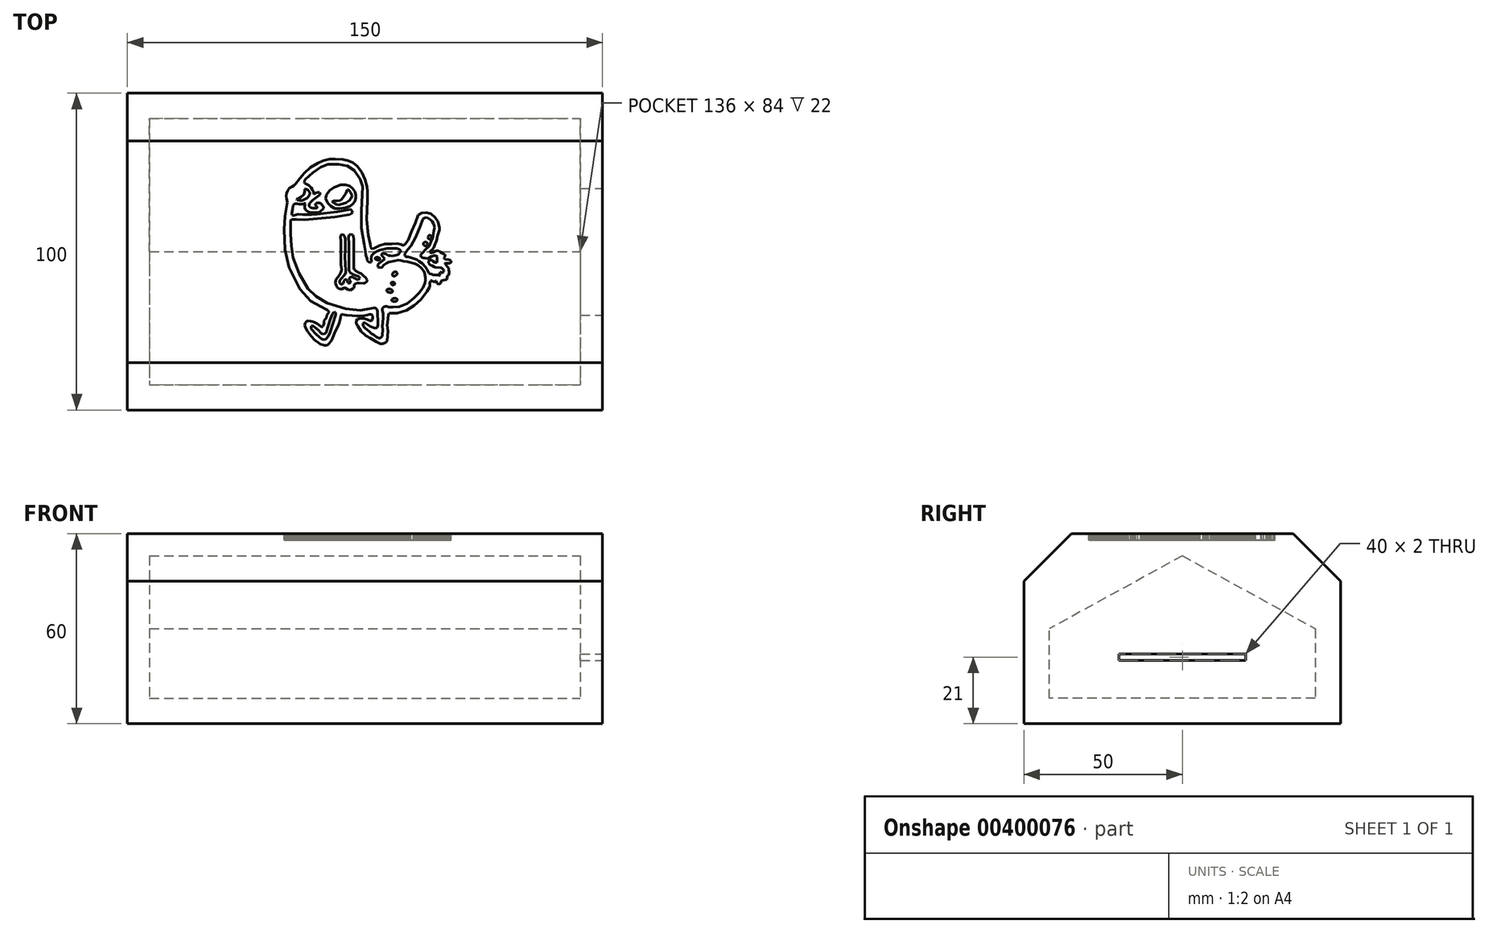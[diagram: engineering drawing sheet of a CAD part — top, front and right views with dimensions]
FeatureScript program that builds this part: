
annotation { "Feature Type Name" : "Feature", "Feature Type Description" : "" }
export const myFeature = defineFeature(function(context is Context, id is Id, definition is map)
    precondition{}
    {
        {
            var Q0;
            Q0=qCreatedBy(makeId("Right.planeOp"),FACE);
            var sketch = newSketch(context, id + "F0", { "sketchPlane" : qUnion([Q0])});
            skLineSegment(sketch, "E0", {"start": v(50, 0) * mm, "end": v(50, -30) * mm});
            skLineSegment(sketch, "E1", {"start": v(50, -30) * mm, "end": v(-50, -30) * mm});
            skLineSegment(sketch, "E2", {"start": v(-50, -30) * mm, "end": v(-50, 30) * mm});
            skLineSegment(sketch, "E3", {"start": v(-50, 30) * mm, "end": v(50, 30) * mm});
            skLineSegment(sketch, "E4", {"start": v(50, 30) * mm, "end": v(50, 0) * mm});
            skLineSegment(sketch, "E5", {"start": v(0, 0) * mm, "end": v(42, 0) * mm});
            skLineSegment(sketch, "E6", {"start": v(42, 0) * mm, "end": v(42, -22) * mm});
            skLineSegment(sketch, "E7", {"start": v(42, -22) * mm, "end": v(-42, -22) * mm});
            skLineSegment(sketch, "E8", {"start": v(-42, -22) * mm, "end": v(-42, 0) * mm});
            skLineSegment(sketch, "E9", {"start": v(0, 30) * mm, "end": v(0, 23) * mm});
            skPoint(sketch, "E9.endSnap0", {"position": v(0, 30) * mm});
            skLineSegment(sketch, "E10", {"start": v(0, 23) * mm, "end": v(-42, 0) * mm});
            skLineSegment(sketch, "E11", {"start": v(0, 23) * mm, "end": v(42, 0) * mm});
            skSolve(sketch);
        }
        {
            var Q0;
            Q0=makeQuery(id+"F0.imprint","IMPRINT",FACE,{"disambiguationData":[TD([[makeQuery(id+"F0.imprint","IMPRINT",EDGE,{"derivedFrom":sQuery(id+"F0.wireOp",EDGE,"E0")}),-1.0]])]});
            extrude(context, id + "F1", {"entities" : qUnion([Q0]), "oppositeDirection" : true, "depth" : 150 * mm});
        }
        {
            var Q0;
            Q0=makeQuery(id+"F1.opExtrude","SWEPT_EDGE",EDGE,{"disambiguationData":[OSD([sQuery(id+"F0.wireOp",EDGE,"E2"),sQuery(id+"F0.wireOp",EDGE,"E3")])]});
            var Q1;
            Q1=makeQuery(id+"F1.opExtrude","SWEPT_EDGE",EDGE,{"disambiguationData":[OSD([sQuery(id+"F0.wireOp",EDGE,"E3"),sQuery(id+"F0.wireOp",EDGE,"E4")])]});
            chamfer(context, id + "F2", {"entities" : qUnion([Q0, Q1]), "width" : 15 * mm, "tangentPropagation" : true});
        }
        {
            var Q0;
            Q0=makeQuery(id+"F1.opExtrude","SWEPT_FACE",FACE,{"disambiguationData":[OSD([sQuery(id+"F0.wireOp",EDGE,"E3")])]});
            var sketch = newSketch(context, id + "F3", { "sketchPlane" : qUnion([Q0])});
            skLineSegment(sketch, "E12", {"start": v(-75, 35) * mm, "end": v(-75, 23.5) * mm});
            skPoint(sketch, "E12.endSnap0", {"position": v(-75, 35) * mm});
            skSolve(sketch);
        }
        {
            var Q0;
            {var subQ0=sQuery(id+"F0.wireOp",EDGE,"E3");var subQ1=makeQuery(id+"F1.opExtrude","CAP_EDGE",EDGE,{"disambiguationData":[OSD([subQ0])],"isStart":true});Q0=makeQuery(id+"F3.imprint","IMPRINT",FACE,{"disambiguationData":[TD([[makeQuery(id+"F3.imprint","IMPRINT",EDGE,{"derivedFrom":subQ1}),1.0]])]});}
            var sketch = newSketch(context, id + "F4", { "sketchPlane" : qUnion([Q0])});
            skLineSegment(sketch, "E13", {"start": v(-75, -30) * mm, "end": v(-105, -30) * mm});
            skLineSegment(sketch, "E14", {"start": v(-105, -30) * mm, "end": v(-105, 30) * mm});
            skLineSegment(sketch, "E15", {"start": v(-105, 30) * mm, "end": v(-45, 30) * mm});
            skLineSegment(sketch, "E16", {"start": v(-71.98, -24.15) * mm, "end": v(-73.3, -23.61) * mm});
            skLineSegment(sketch, "E17", {"start": v(-73.3, -23.61) * mm, "end": v(-74.24, -22.99) * mm});
            skLineSegment(sketch, "E18", {"start": v(-74.24, -22.99) * mm, "end": v(-74.66, -22.67) * mm});
            skLineSegment(sketch, "E19", {"start": v(-74.66, -22.67) * mm, "end": v(-75, -22.48) * mm});
            skLineSegment(sketch, "E20", {"start": v(-75, -22.48) * mm, "end": v(-75.21, -22.4) * mm});
            skLineSegment(sketch, "E21", {"start": v(-75.21, -22.4) * mm, "end": v(-75.4, -22.46) * mm});
            skLineSegment(sketch, "E22", {"start": v(-75.4, -22.46) * mm, "end": v(-75.59, -22.63) * mm});
            skLineSegment(sketch, "E23", {"start": v(-75.59, -22.63) * mm, "end": v(-75.65, -22.8) * mm});
            skLineSegment(sketch, "E24", {"start": v(-75.65, -22.8) * mm, "end": v(-75.62, -23.14) * mm});
            skLineSegment(sketch, "E25", {"start": v(-75.62, -23.14) * mm, "end": v(-75.54, -23.43) * mm});
            skLineSegment(sketch, "E26", {"start": v(-75.54, -23.43) * mm, "end": v(-75.46, -23.63) * mm});
            skLineSegment(sketch, "E27", {"start": v(-75.46, -23.63) * mm, "end": v(-75.27, -23.87) * mm});
            skLineSegment(sketch, "E28", {"start": v(-75.27, -23.87) * mm, "end": v(-74.9, -24.18) * mm});
            skLineSegment(sketch, "E29", {"start": v(-74.9, -24.18) * mm, "end": v(-74.4, -24.63) * mm});
            skLineSegment(sketch, "E30", {"start": v(-74.4, -24.63) * mm, "end": v(-73.63, -25.23) * mm});
            skLineSegment(sketch, "E31", {"start": v(-73.63, -25.23) * mm, "end": v(-73.29, -25.57) * mm});
            skLineSegment(sketch, "E32", {"start": v(-73.29, -25.57) * mm, "end": v(-72.93, -25.92) * mm});
            skLineSegment(sketch, "E33", {"start": v(-72.93, -25.92) * mm, "end": v(-72.2, -26.3) * mm});
            skLineSegment(sketch, "E34", {"start": v(-72.2, -26.3) * mm, "end": v(-71.39, -26.84) * mm});
            skLineSegment(sketch, "E35", {"start": v(-71.39, -26.84) * mm, "end": v(-70.97, -27.16) * mm});
            skLineSegment(sketch, "E36", {"start": v(-70.97, -27.16) * mm, "end": v(-70.75, -27.24) * mm});
            skLineSegment(sketch, "E37", {"start": v(-70.75, -27.24) * mm, "end": v(-70.5, -27.26) * mm});
            skLineSegment(sketch, "E38", {"start": v(-70.5, -27.26) * mm, "end": v(-70.2, -27.24) * mm});
            skLineSegment(sketch, "E39", {"start": v(-70.2, -27.24) * mm, "end": v(-70, -27.13) * mm});
            skLineSegment(sketch, "E40", {"start": v(-70, -27.13) * mm, "end": v(-69.78, -26.94) * mm});
            skLineSegment(sketch, "E41", {"start": v(-69.78, -26.94) * mm, "end": v(-69.61, -26.76) * mm});
            skLineSegment(sketch, "E42", {"start": v(-69.61, -26.76) * mm, "end": v(-69.59, -26.59) * mm});
            skLineSegment(sketch, "E43", {"start": v(-69.59, -26.59) * mm, "end": v(-69.59, -26.2) * mm});
            skLineSegment(sketch, "E44", {"start": v(-69.59, -26.2) * mm, "end": v(-69.38, -24.72) * mm});
            skLineSegment(sketch, "E45", {"start": v(-69.38, -24.72) * mm, "end": v(-69.38, -24.43) * mm});
            skLineSegment(sketch, "E46", {"start": v(-69.38, -24.43) * mm, "end": v(-69.59, -23.58) * mm});
            skLineSegment(sketch, "E47", {"start": v(-69.59, -23.58) * mm, "end": v(-69.59, -23.26) * mm});
            skLineSegment(sketch, "E48", {"start": v(-69.59, -23.26) * mm, "end": v(-69.43, -22.71) * mm});
            skLineSegment(sketch, "E49", {"start": v(-69.43, -22.71) * mm, "end": v(-69.43, -22.14) * mm});
            skLineSegment(sketch, "E50", {"start": v(-69.43, -22.14) * mm, "end": v(-69.32, -21.24) * mm});
            skLineSegment(sketch, "E51", {"start": v(-69.32, -21.24) * mm, "end": v(-69.32, -20.77) * mm});
            skLineSegment(sketch, "E52", {"start": v(-69.32, -20.77) * mm, "end": v(-69.32, -20.27) * mm});
            skLineSegment(sketch, "E53", {"start": v(-69.32, -20.27) * mm, "end": v(-69.32, -19.5) * mm});
            skLineSegment(sketch, "E54", {"start": v(-69.32, -19.5) * mm, "end": v(-69.48, -18.45) * mm});
            skLineSegment(sketch, "E55", {"start": v(-69.48, -18.45) * mm, "end": v(-69.48, -17.95) * mm});
            skLineSegment(sketch, "E56", {"start": v(-69.48, -17.95) * mm, "end": v(-69.36, -17.76) * mm});
            skLineSegment(sketch, "E57", {"start": v(-69.36, -17.76) * mm, "end": v(-69.13, -17.52) * mm});
            skLineSegment(sketch, "E58", {"start": v(-69.13, -17.52) * mm, "end": v(-68.89, -17.36) * mm});
            skLineSegment(sketch, "E59", {"start": v(-68.89, -17.36) * mm, "end": v(-68.51, -17.3) * mm});
            skLineSegment(sketch, "E60", {"start": v(-68.51, -17.3) * mm, "end": v(-68.18, -17.3) * mm});
            skLineSegment(sketch, "E61", {"start": v(-68.18, -17.3) * mm, "end": v(-67.9, -17.38) * mm});
            skLineSegment(sketch, "E62", {"start": v(-67.9, -17.38) * mm, "end": v(-67.48, -17.5) * mm});
            skLineSegment(sketch, "E63", {"start": v(-67.48, -17.5) * mm, "end": v(-66.25, -17.5) * mm});
            skLineSegment(sketch, "E64", {"start": v(-66.25, -17.5) * mm, "end": v(-64.2, -17.36) * mm});
            skLineSegment(sketch, "E65", {"start": v(-64.2, -17.36) * mm, "end": v(-61.7, -16.34) * mm});
            skLineSegment(sketch, "E66", {"start": v(-61.7, -16.34) * mm, "end": v(-59.52, -14.64) * mm});
            skLineSegment(sketch, "E67", {"start": v(-59.52, -14.64) * mm, "end": v(-57.93, -13.11) * mm});
            skLineSegment(sketch, "E68", {"start": v(-57.93, -13.11) * mm, "end": v(-56.69, -11.42) * mm});
            skLineSegment(sketch, "E69", {"start": v(-56.69, -11.42) * mm, "end": v(-56.02, -9.86) * mm});
            skLineSegment(sketch, "E70", {"start": v(-56.02, -9.86) * mm, "end": v(-55.91, -8.97) * mm});
            skLineSegment(sketch, "E71", {"start": v(-55.91, -8.97) * mm, "end": v(-55.91, -8.12) * mm});
            skLineSegment(sketch, "E72", {"start": v(-55.91, -8.12) * mm, "end": v(-56.24, -6.75) * mm});
            skLineSegment(sketch, "E73", {"start": v(-56.24, -6.75) * mm, "end": v(-56.49, -6.12) * mm});
            skLineSegment(sketch, "E74", {"start": v(-56.49, -6.12) * mm, "end": v(-57.35, -5.03) * mm});
            skLineSegment(sketch, "E75", {"start": v(-57.35, -5.03) * mm, "end": v(-58.23, -4.36) * mm});
            skLineSegment(sketch, "E76", {"start": v(-58.23, -4.36) * mm, "end": v(-59.3, -3.85) * mm});
            skLineSegment(sketch, "E77", {"start": v(-59.3, -3.85) * mm, "end": v(-60.49, -3.51) * mm});
            skLineSegment(sketch, "E78", {"start": v(-60.49, -3.51) * mm, "end": v(-61.7, -3.16) * mm});
            skLineSegment(sketch, "E79", {"start": v(-61.7, -3.16) * mm, "end": v(-62.84, -3.03) * mm});
            skLineSegment(sketch, "E80", {"start": v(-62.84, -3.03) * mm, "end": v(-63.68, -2.8) * mm});
            skLineSegment(sketch, "E81", {"start": v(-63.68, -2.8) * mm, "end": v(-64.49, -2.68) * mm});
            skLineSegment(sketch, "E82", {"start": v(-64.49, -2.68) * mm, "end": v(-65.55, -2.88) * mm});
            skLineSegment(sketch, "E83", {"start": v(-65.55, -2.88) * mm, "end": v(-66.86, -3.15) * mm});
            skLineSegment(sketch, "E84", {"start": v(-66.86, -3.15) * mm, "end": v(-67.54, -3.32) * mm});
            skLineSegment(sketch, "E85", {"start": v(-67.54, -3.32) * mm, "end": v(-68.24, -3.7) * mm});
            skLineSegment(sketch, "E86", {"start": v(-68.24, -3.7) * mm, "end": v(-68.99, -4.16) * mm});
            skLineSegment(sketch, "E87", {"start": v(-68.99, -4.16) * mm, "end": v(-69.7, -4.92) * mm});
            skLineSegment(sketch, "E88", {"start": v(-69.7, -4.92) * mm, "end": v(-70.2, -5.03) * mm});
            skLineSegment(sketch, "E89", {"start": v(-70.2, -5.03) * mm, "end": v(-70.78, -4.93) * mm});
            skLineSegment(sketch, "E90", {"start": v(-70.78, -4.93) * mm, "end": v(-70.95, -4.48) * mm});
            skLineSegment(sketch, "E91", {"start": v(-70.95, -4.48) * mm, "end": v(-70.88, -4.03) * mm});
            skLineSegment(sketch, "E92", {"start": v(-70.88, -4.03) * mm, "end": v(-70.5, -3.62) * mm});
            skLineSegment(sketch, "E93", {"start": v(-70.5, -3.62) * mm, "end": v(-69.59, -2.91) * mm});
            skLineSegment(sketch, "E94", {"start": v(-69.59, -2.91) * mm, "end": v(-69.06, -2.52) * mm});
            skLineSegment(sketch, "E95", {"start": v(-69.06, -2.52) * mm, "end": v(-68.87, -2.37) * mm});
            skLineSegment(sketch, "E96", {"start": v(-68.87, -2.37) * mm, "end": v(-68.8, -2.22) * mm});
            skLineSegment(sketch, "E97", {"start": v(-68.8, -2.22) * mm, "end": v(-68.85, -2.09) * mm});
            skLineSegment(sketch, "E98", {"start": v(-68.85, -2.09) * mm, "end": v(-69.21, -1.74) * mm});
            skLineSegment(sketch, "E99", {"start": v(-69.21, -1.74) * mm, "end": v(-69.55, -1.41) * mm});
            skLineSegment(sketch, "E100", {"start": v(-69.55, -1.41) * mm, "end": v(-69.78, -1.12) * mm});
            skLineSegment(sketch, "E101", {"start": v(-69.78, -1.12) * mm, "end": v(-69.78, -0.84) * mm});
            skLineSegment(sketch, "E102", {"start": v(-69.78, -0.84) * mm, "end": v(-69.59, -0.64) * mm});
            skLineSegment(sketch, "E103", {"start": v(-69.59, -0.64) * mm, "end": v(-69.28, -0.53) * mm});
            skLineSegment(sketch, "E104", {"start": v(-69.28, -0.53) * mm, "end": v(-68.85, -0.57) * mm});
            skLineSegment(sketch, "E105", {"start": v(-68.85, -0.57) * mm, "end": v(-68.35, -0.77) * mm});
            skLineSegment(sketch, "E106", {"start": v(-68.35, -0.77) * mm, "end": v(-67.91, -1.05) * mm});
            skLineSegment(sketch, "E107", {"start": v(-67.91, -1.05) * mm, "end": v(-67.66, -1.2) * mm});
            skLineSegment(sketch, "E108", {"start": v(-67.66, -1.2) * mm, "end": v(-67.12, -1.31) * mm});
            skLineSegment(sketch, "E109", {"start": v(-67.12, -1.31) * mm, "end": v(-66.48, -1.36) * mm});
            skLineSegment(sketch, "E110", {"start": v(-66.48, -1.36) * mm, "end": v(-65.85, -1.29) * mm});
            skLineSegment(sketch, "E111", {"start": v(-65.85, -1.29) * mm, "end": v(-65.16, -1.1) * mm});
            skLineSegment(sketch, "E112", {"start": v(-65.16, -1.1) * mm, "end": v(-64.4, -0.83) * mm});
            skLineSegment(sketch, "E113", {"start": v(-64.4, -0.83) * mm, "end": v(-64, -0.41) * mm});
            skLineSegment(sketch, "E114", {"start": v(-64, -0.41) * mm, "end": v(-63.77, -0.05) * mm});
            skLineSegment(sketch, "E115", {"start": v(-63.77, -0.05) * mm, "end": v(-63.67, 0.12) * mm});
            skLineSegment(sketch, "E116", {"start": v(-63.67, 0.12) * mm, "end": v(-63.67, 0.25) * mm});
            skLineSegment(sketch, "E117", {"start": v(-63.67, 0.25) * mm, "end": v(-63.8, 0.42) * mm});
            skLineSegment(sketch, "E118", {"start": v(-63.8, 0.42) * mm, "end": v(-64.05, 0.66) * mm});
            skLineSegment(sketch, "E119", {"start": v(-64.05, 0.66) * mm, "end": v(-64.33, 0.83) * mm});
            skLineSegment(sketch, "E120", {"start": v(-64.33, 0.83) * mm, "end": v(-65, 1.01) * mm});
            skLineSegment(sketch, "E121", {"start": v(-65, 1.01) * mm, "end": v(-67.97, 1.01) * mm});
            skLineSegment(sketch, "E122", {"start": v(-67.97, 1.01) * mm, "end": v(-70.15, 0.5) * mm});
            skLineSegment(sketch, "E123", {"start": v(-70.15, 0.5) * mm, "end": v(-71.15, 0.09) * mm});
            skLineSegment(sketch, "E124", {"start": v(-71.15, 0.09) * mm, "end": v(-72.04, -0.39) * mm});
            skLineSegment(sketch, "E125", {"start": v(-72.04, -0.39) * mm, "end": v(-72.9, -1.27) * mm});
            skLineSegment(sketch, "E126", {"start": v(-72.9, -1.27) * mm, "end": v(-73, -1.55) * mm});
            skLineSegment(sketch, "E127", {"start": v(-73, -1.55) * mm, "end": v(-73.1, -2.31) * mm});
            skLineSegment(sketch, "E128", {"start": v(-73.1, -2.31) * mm, "end": v(-73, -2.78) * mm});
            skLineSegment(sketch, "E129", {"start": v(-73, -2.78) * mm, "end": v(-72.95, -3.06) * mm});
            skLineSegment(sketch, "E130", {"start": v(-72.95, -3.06) * mm, "end": v(-73.07, -3.26) * mm});
            skLineSegment(sketch, "E131", {"start": v(-73.07, -3.26) * mm, "end": v(-73.32, -3.38) * mm});
            skLineSegment(sketch, "E132", {"start": v(-73.32, -3.38) * mm, "end": v(-73.7, -3.3) * mm});
            skLineSegment(sketch, "E133", {"start": v(-73.7, -3.3) * mm, "end": v(-74.07, -3.07) * mm});
            skLineSegment(sketch, "E134", {"start": v(-74.07, -3.07) * mm, "end": v(-74.3, -2.59) * mm});
            skLineSegment(sketch, "E135", {"start": v(-74.3, -2.59) * mm, "end": v(-74.3, -2.1) * mm});
            skLineSegment(sketch, "E136", {"start": v(-74.3, -2.1) * mm, "end": v(-74.7, -1.15) * mm});
            skLineSegment(sketch, "E137", {"start": v(-74.7, -1.15) * mm, "end": v(-74.8, 0) * mm});
            skLineSegment(sketch, "E138", {"start": v(-74.8, 0) * mm, "end": v(-75.18, 2.3) * mm});
            skLineSegment(sketch, "E139", {"start": v(-75.18, 2.3) * mm, "end": v(-76.2, 7.42) * mm});
            skLineSegment(sketch, "E140", {"start": v(-76.2, 7.42) * mm, "end": v(-76.2, 12.88) * mm});
            skLineSegment(sketch, "E141", {"start": v(-76.2, 12.88) * mm, "end": v(-76, 16.85) * mm});
            skLineSegment(sketch, "E142", {"start": v(-76, 16.85) * mm, "end": v(-75.8, 20.59) * mm});
            skLineSegment(sketch, "E143", {"start": v(-75.8, 20.59) * mm, "end": v(-76.53, 22.91) * mm});
            skLineSegment(sketch, "E144", {"start": v(-76.53, 22.91) * mm, "end": v(-78.47, 25.72) * mm});
            skLineSegment(sketch, "E145", {"start": v(-78.47, 25.72) * mm, "end": v(-80.63, 27.07) * mm});
            skLineSegment(sketch, "E146", {"start": v(-80.63, 27.07) * mm, "end": v(-83.35, 27.56) * mm});
            skLineSegment(sketch, "E147", {"start": v(-83.35, 27.56) * mm, "end": v(-86.64, 27.56) * mm});
            skLineSegment(sketch, "E148", {"start": v(-86.64, 27.56) * mm, "end": v(-88.91, 26.63) * mm});
            skLineSegment(sketch, "E149", {"start": v(-88.91, 26.63) * mm, "end": v(-91.46, 24.93) * mm});
            skLineSegment(sketch, "E150", {"start": v(-91.46, 24.93) * mm, "end": v(-93.75, 22.9) * mm});
            skLineSegment(sketch, "E151", {"start": v(-93.75, 22.9) * mm, "end": v(-94.04, 22.5) * mm});
            skLineSegment(sketch, "E152", {"start": v(-94.04, 22.5) * mm, "end": v(-94.19, 22.02) * mm});
            skLineSegment(sketch, "E153", {"start": v(-94.19, 22.02) * mm, "end": v(-94.06, 21.65) * mm});
            skLineSegment(sketch, "E154", {"start": v(-94.06, 21.65) * mm, "end": v(-93.48, 21.4) * mm});
            skLineSegment(sketch, "E155", {"start": v(-93.48, 21.4) * mm, "end": v(-92.7, 20.95) * mm});
            skLineSegment(sketch, "E156", {"start": v(-92.7, 20.95) * mm, "end": v(-92.05, 20.22) * mm});
            skLineSegment(sketch, "E157", {"start": v(-92.05, 20.22) * mm, "end": v(-91.63, 19.6) * mm});
            skLineSegment(sketch, "E158", {"start": v(-91.63, 19.6) * mm, "end": v(-91.26, 18.75) * mm});
            skLineSegment(sketch, "E159", {"start": v(-91.26, 18.75) * mm, "end": v(-91.26, 18.5) * mm});
            skLineSegment(sketch, "E160", {"start": v(-91.26, 18.5) * mm, "end": v(-91.2, 18.3) * mm});
            skLineSegment(sketch, "E161", {"start": v(-91.2, 18.3) * mm, "end": v(-91.07, 18.21) * mm});
            skLineSegment(sketch, "E162", {"start": v(-91.07, 18.21) * mm, "end": v(-90.87, 18.28) * mm});
            skLineSegment(sketch, "E163", {"start": v(-90.87, 18.28) * mm, "end": v(-90.53, 18.5) * mm});
            skLineSegment(sketch, "E164", {"start": v(-90.53, 18.5) * mm, "end": v(-89.92, 18.75) * mm});
            skLineSegment(sketch, "E165", {"start": v(-89.92, 18.75) * mm, "end": v(-89.58, 18.75) * mm});
            skLineSegment(sketch, "E166", {"start": v(-89.58, 18.75) * mm, "end": v(-89.34, 18.63) * mm});
            skLineSegment(sketch, "E167", {"start": v(-89.34, 18.63) * mm, "end": v(-89.23, 18.46) * mm});
            skLineSegment(sketch, "E168", {"start": v(-89.23, 18.46) * mm, "end": v(-89.2, 18.17) * mm});
            skLineSegment(sketch, "E169", {"start": v(-89.2, 18.17) * mm, "end": v(-89.26, 17.96) * mm});
            skLineSegment(sketch, "E170", {"start": v(-89.26, 17.96) * mm, "end": v(-89.44, 17.78) * mm});
            skLineSegment(sketch, "E171", {"start": v(-89.44, 17.78) * mm, "end": v(-90.57, 16.9) * mm});
            skLineSegment(sketch, "E172", {"start": v(-90.57, 16.9) * mm, "end": v(-91.46, 16.22) * mm});
            skLineSegment(sketch, "E173", {"start": v(-91.46, 16.22) * mm, "end": v(-92.4, 15.35) * mm});
            skLineSegment(sketch, "E174", {"start": v(-92.4, 15.35) * mm, "end": v(-92.51, 15.1) * mm});
            skLineSegment(sketch, "E175", {"start": v(-92.51, 15.1) * mm, "end": v(-92.6, 14.76) * mm});
            skLineSegment(sketch, "E176", {"start": v(-92.6, 14.76) * mm, "end": v(-92.6, 14.39) * mm});
            skLineSegment(sketch, "E177", {"start": v(-92.6, 14.39) * mm, "end": v(-92.4, 14.1) * mm});
            skLineSegment(sketch, "E178", {"start": v(-92.4, 14.1) * mm, "end": v(-92.05, 13.83) * mm});
            skLineSegment(sketch, "E179", {"start": v(-92.05, 13.83) * mm, "end": v(-91.56, 13.75) * mm});
            skLineSegment(sketch, "E180", {"start": v(-91.56, 13.75) * mm, "end": v(-90.86, 13.75) * mm});
            skLineSegment(sketch, "E181", {"start": v(-90.86, 13.75) * mm, "end": v(-90.22, 13.75) * mm});
            skLineSegment(sketch, "E182", {"start": v(-90.22, 13.75) * mm, "end": v(-90.12, 13.83) * mm});
            skLineSegment(sketch, "E183", {"start": v(-90.12, 13.83) * mm, "end": v(-90.06, 13.99) * mm});
            skLineSegment(sketch, "E184", {"start": v(-90.06, 13.99) * mm, "end": v(-90.1, 14.08) * mm});
            skLineSegment(sketch, "E185", {"start": v(-90.1, 14.08) * mm, "end": v(-90.36, 14.31) * mm});
            skLineSegment(sketch, "E186", {"start": v(-90.36, 14.31) * mm, "end": v(-90.58, 14.57) * mm});
            skLineSegment(sketch, "E187", {"start": v(-90.58, 14.57) * mm, "end": v(-90.64, 14.84) * mm});
            skLineSegment(sketch, "E188", {"start": v(-90.64, 14.84) * mm, "end": v(-90.6, 15.06) * mm});
            skLineSegment(sketch, "E189", {"start": v(-90.6, 15.06) * mm, "end": v(-90.45, 15.24) * mm});
            skLineSegment(sketch, "E190", {"start": v(-90.45, 15.24) * mm, "end": v(-90.12, 15.37) * mm});
            skLineSegment(sketch, "E191", {"start": v(-90.12, 15.37) * mm, "end": v(-89.72, 15.42) * mm});
            skLineSegment(sketch, "E192", {"start": v(-89.72, 15.42) * mm, "end": v(-89.3, 15.34) * mm});
            skLineSegment(sketch, "E193", {"start": v(-89.3, 15.34) * mm, "end": v(-89.02, 15.25) * mm});
            skLineSegment(sketch, "E194", {"start": v(-89.02, 15.25) * mm, "end": v(-88.87, 15.12) * mm});
            skLineSegment(sketch, "E195", {"start": v(-88.87, 15.12) * mm, "end": v(-88.55, 14.81) * mm});
            skLineSegment(sketch, "E196", {"start": v(-88.55, 14.81) * mm, "end": v(-88.29, 14.45) * mm});
            skLineSegment(sketch, "E197", {"start": v(-88.29, 14.45) * mm, "end": v(-88.13, 13.99) * mm});
            skLineSegment(sketch, "E198", {"start": v(-88.13, 13.99) * mm, "end": v(-88.1, 13.78) * mm});
            skLineSegment(sketch, "E199", {"start": v(-88.1, 13.78) * mm, "end": v(-88.15, 13.62) * mm});
            skLineSegment(sketch, "E200", {"start": v(-88.15, 13.62) * mm, "end": v(-88.36, 13.31) * mm});
            skLineSegment(sketch, "E201", {"start": v(-88.36, 13.31) * mm, "end": v(-88.92, 12.84) * mm});
            skLineSegment(sketch, "E202", {"start": v(-88.92, 12.84) * mm, "end": v(-89.48, 12.46) * mm});
            skLineSegment(sketch, "E203", {"start": v(-89.48, 12.46) * mm, "end": v(-89.66, 12.35) * mm});
            skLineSegment(sketch, "E204", {"start": v(-89.66, 12.35) * mm, "end": v(-90.12, 12.3) * mm});
            skLineSegment(sketch, "E205", {"start": v(-90.12, 12.3) * mm, "end": v(-91.09, 12.3) * mm});
            skLineSegment(sketch, "E206", {"start": v(-91.09, 12.3) * mm, "end": v(-92.27, 12.35) * mm});
            skLineSegment(sketch, "E207", {"start": v(-92.27, 12.35) * mm, "end": v(-93.13, 12.77) * mm});
            skLineSegment(sketch, "E208", {"start": v(-93.13, 12.77) * mm, "end": v(-93.72, 13.25) * mm});
            skLineSegment(sketch, "E209", {"start": v(-93.72, 13.25) * mm, "end": v(-94.02, 13.88) * mm});
            skLineSegment(sketch, "E210", {"start": v(-94.02, 13.88) * mm, "end": v(-94.1, 14.4) * mm});
            skLineSegment(sketch, "E211", {"start": v(-94.1, 14.4) * mm, "end": v(-93.87, 14.95) * mm});
            skLineSegment(sketch, "E212", {"start": v(-93.87, 14.95) * mm, "end": v(-93.82, 15.16) * mm});
            skLineSegment(sketch, "E213", {"start": v(-93.82, 15.16) * mm, "end": v(-93.85, 15.23) * mm});
            skLineSegment(sketch, "E214", {"start": v(-93.85, 15.23) * mm, "end": v(-93.93, 15.25) * mm});
            skLineSegment(sketch, "E215", {"start": v(-93.93, 15.25) * mm, "end": v(-94.06, 15.21) * mm});
            skLineSegment(sketch, "E216", {"start": v(-94.06, 15.21) * mm, "end": v(-94.24, 15.07) * mm});
            skLineSegment(sketch, "E217", {"start": v(-94.24, 15.07) * mm, "end": v(-94.44, 15.03) * mm});
            skLineSegment(sketch, "E218", {"start": v(-94.44, 15.03) * mm, "end": v(-94.87, 15.03) * mm});
            skLineSegment(sketch, "E219", {"start": v(-94.87, 15.03) * mm, "end": v(-95.85, 14.97) * mm});
            skLineSegment(sketch, "E220", {"start": v(-95.85, 14.97) * mm, "end": v(-96.37, 15.09) * mm});
            skLineSegment(sketch, "E221", {"start": v(-96.37, 15.09) * mm, "end": v(-96.9, 15.16) * mm});
            skLineSegment(sketch, "E222", {"start": v(-96.9, 15.16) * mm, "end": v(-97.21, 15.09) * mm});
            skLineSegment(sketch, "E223", {"start": v(-97.21, 15.09) * mm, "end": v(-97.5, 14.88) * mm});
            skLineSegment(sketch, "E224", {"start": v(-97.5, 14.88) * mm, "end": v(-97.77, 14.52) * mm});
            skLineSegment(sketch, "E225", {"start": v(-97.77, 14.52) * mm, "end": v(-97.88, 13.48) * mm});
            skLineSegment(sketch, "E226", {"start": v(-97.88, 13.48) * mm, "end": v(-98.11, 12.04) * mm});
            skLineSegment(sketch, "E227", {"start": v(-98.11, 12.04) * mm, "end": v(-98.07, 11.83) * mm});
            skLineSegment(sketch, "E228", {"start": v(-98.07, 11.83) * mm, "end": v(-97.93, 11.6) * mm});
            skLineSegment(sketch, "E229", {"start": v(-97.93, 11.6) * mm, "end": v(-97.76, 11.48) * mm});
            skLineSegment(sketch, "E230", {"start": v(-97.76, 11.48) * mm, "end": v(-97.47, 11.48) * mm});
            skLineSegment(sketch, "E231", {"start": v(-97.47, 11.48) * mm, "end": v(-96.04, 11.86) * mm});
            skLineSegment(sketch, "E232", {"start": v(-96.04, 11.86) * mm, "end": v(-94.63, 11.75) * mm});
            skLineSegment(sketch, "E233", {"start": v(-94.63, 11.75) * mm, "end": v(-93.17, 11.75) * mm});
            skLineSegment(sketch, "E234", {"start": v(-93.17, 11.75) * mm, "end": v(-91.82, 11.68) * mm});
            skLineSegment(sketch, "E235", {"start": v(-91.82, 11.68) * mm, "end": v(-90.06, 11.8) * mm});
            skLineSegment(sketch, "E236", {"start": v(-90.06, 11.8) * mm, "end": v(-88.1, 12.06) * mm});
            skLineSegment(sketch, "E237", {"start": v(-88.1, 12.06) * mm, "end": v(-83.76, 12.59) * mm});
            skLineSegment(sketch, "E238", {"start": v(-83.76, 12.59) * mm, "end": v(-79.74, 13.3) * mm});
            skLineSegment(sketch, "E239", {"start": v(-79.74, 13.3) * mm, "end": v(-79.4, 13.22) * mm});
            skLineSegment(sketch, "E240", {"start": v(-79.4, 13.22) * mm, "end": v(-79.14, 13) * mm});
            skLineSegment(sketch, "E241", {"start": v(-79.14, 13) * mm, "end": v(-79, 12.69) * mm});
            skLineSegment(sketch, "E242", {"start": v(-79, 12.69) * mm, "end": v(-78.97, 12.38) * mm});
            skLineSegment(sketch, "E243", {"start": v(-78.97, 12.38) * mm, "end": v(-79.09, 12.16) * mm});
            skLineSegment(sketch, "E244", {"start": v(-79.09, 12.16) * mm, "end": v(-79.4, 11.9) * mm});
            skLineSegment(sketch, "E245", {"start": v(-79.4, 11.9) * mm, "end": v(-79.81, 11.7) * mm});
            skLineSegment(sketch, "E246", {"start": v(-79.81, 11.7) * mm, "end": v(-80.64, 11.6) * mm});
            skLineSegment(sketch, "E247", {"start": v(-80.64, 11.6) * mm, "end": v(-84.55, 10.93) * mm});
            skLineSegment(sketch, "E248", {"start": v(-84.55, 10.93) * mm, "end": v(-94.17, 10.06) * mm});
            skLineSegment(sketch, "E249", {"start": v(-94.17, 10.06) * mm, "end": v(-96.58, 10.24) * mm});
            skLineSegment(sketch, "E250", {"start": v(-96.58, 10.24) * mm, "end": v(-98.07, 10.14) * mm});
            skLineSegment(sketch, "E251", {"start": v(-98.07, 10.14) * mm, "end": v(-98.45, 9.9) * mm});
            skLineSegment(sketch, "E252", {"start": v(-98.45, 9.9) * mm, "end": v(-98.52, 9.36) * mm});
            skLineSegment(sketch, "E253", {"start": v(-98.52, 9.36) * mm, "end": v(-98.45, 8.32) * mm});
            skLineSegment(sketch, "E254", {"start": v(-98.45, 8.32) * mm, "end": v(-98.45, 5.66) * mm});
            skLineSegment(sketch, "E255", {"start": v(-98.45, 5.66) * mm, "end": v(-98.2, 1.8) * mm});
            skLineSegment(sketch, "E256", {"start": v(-98.2, 1.8) * mm, "end": v(-97.72, -1.94) * mm});
            skLineSegment(sketch, "E257", {"start": v(-97.72, -1.94) * mm, "end": v(-95.87, -6.83) * mm});
            skLineSegment(sketch, "E258", {"start": v(-95.87, -6.83) * mm, "end": v(-93.01, -11.66) * mm});
            skLineSegment(sketch, "E259", {"start": v(-93.01, -11.66) * mm, "end": v(-90.52, -14.09) * mm});
            skLineSegment(sketch, "E260", {"start": v(-90.52, -14.09) * mm, "end": v(-86.88, -16.22) * mm});
            skLineSegment(sketch, "E261", {"start": v(-86.88, -16.22) * mm, "end": v(-81.1, -17.98) * mm});
            skLineSegment(sketch, "E262", {"start": v(-81.1, -17.98) * mm, "end": v(-76.47, -18.57) * mm});
            skLineSegment(sketch, "E263", {"start": v(-76.47, -18.57) * mm, "end": v(-72.2, -17.82) * mm});
            skLineSegment(sketch, "E264", {"start": v(-72.2, -17.82) * mm, "end": v(-71.83, -17.82) * mm});
            skLineSegment(sketch, "E265", {"start": v(-71.83, -17.82) * mm, "end": v(-71.56, -17.88) * mm});
            skLineSegment(sketch, "E266", {"start": v(-71.56, -17.88) * mm, "end": v(-71.3, -18.12) * mm});
            skLineSegment(sketch, "E267", {"start": v(-71.3, -18.12) * mm, "end": v(-71.14, -18.4) * mm});
            skLineSegment(sketch, "E268", {"start": v(-71.14, -18.4) * mm, "end": v(-71.07, -18.9) * mm});
            skLineSegment(sketch, "E269", {"start": v(-71.07, -18.9) * mm, "end": v(-71.07, -20.2) * mm});
            skLineSegment(sketch, "E270", {"start": v(-71.07, -20.2) * mm, "end": v(-70.98, -21.49) * mm});
            skLineSegment(sketch, "E271", {"start": v(-70.98, -21.49) * mm, "end": v(-70.98, -21.97) * mm});
            skLineSegment(sketch, "E272", {"start": v(-70.98, -21.97) * mm, "end": v(-70.98, -23.26) * mm});
            skLineSegment(sketch, "E273", {"start": v(-70.98, -23.26) * mm, "end": v(-71.03, -23.66) * mm});
            skLineSegment(sketch, "E274", {"start": v(-71.03, -23.66) * mm, "end": v(-71.23, -23.95) * mm});
            skLineSegment(sketch, "E275", {"start": v(-71.23, -23.95) * mm, "end": v(-71.5, -24.12) * mm});
            skLineSegment(sketch, "E276", {"start": v(-71.5, -24.12) * mm, "end": v(-71.72, -24.18) * mm});
            skLineSegment(sketch, "E277", {"start": v(-71.72, -24.18) * mm, "end": v(-71.98, -24.15) * mm});
            skLineSegment(sketch, "E278", {"start": v(-81.15, 4.1) * mm, "end": v(-81.15, 0.56) * mm});
            skLineSegment(sketch, "E279", {"start": v(-81.15, 0.56) * mm, "end": v(-81.32, -1.54) * mm});
            skLineSegment(sketch, "E280", {"start": v(-81.32, -1.54) * mm, "end": v(-81.2, -4.03) * mm});
            skLineSegment(sketch, "E281", {"start": v(-81.2, -4.03) * mm, "end": v(-81.03, -5.77) * mm});
            skLineSegment(sketch, "E282", {"start": v(-81.03, -5.77) * mm, "end": v(-81.03, -6.64) * mm});
            skLineSegment(sketch, "E283", {"start": v(-81.03, -6.64) * mm, "end": v(-81.29, -7.22) * mm});
            skLineSegment(sketch, "E284", {"start": v(-81.29, -7.22) * mm, "end": v(-82.78, -8.8) * mm});
            skLineSegment(sketch, "E285", {"start": v(-82.78, -8.8) * mm, "end": v(-82.98, -9.25) * mm});
            skLineSegment(sketch, "E286", {"start": v(-82.98, -9.25) * mm, "end": v(-83.04, -9.73) * mm});
            skLineSegment(sketch, "E287", {"start": v(-83.04, -9.73) * mm, "end": v(-82.88, -10.05) * mm});
            skLineSegment(sketch, "E288", {"start": v(-82.88, -10.05) * mm, "end": v(-82.6, -10.23) * mm});
            skLineSegment(sketch, "E289", {"start": v(-82.6, -10.23) * mm, "end": v(-82.3, -10.23) * mm});
            skLineSegment(sketch, "E290", {"start": v(-82.3, -10.23) * mm, "end": v(-81.85, -9.97) * mm});
            skLineSegment(sketch, "E291", {"start": v(-81.85, -9.97) * mm, "end": v(-81.74, -9.38) * mm});
            skLineSegment(sketch, "E292", {"start": v(-81.74, -9.38) * mm, "end": v(-81.52, -8.97) * mm});
            skLineSegment(sketch, "E293", {"start": v(-81.52, -8.97) * mm, "end": v(-81.16, -8.75) * mm});
            skLineSegment(sketch, "E294", {"start": v(-81.16, -8.75) * mm, "end": v(-80.91, -8.75) * mm});
            skLineSegment(sketch, "E295", {"start": v(-80.91, -8.75) * mm, "end": v(-80.64, -9.22) * mm});
            skLineSegment(sketch, "E296", {"start": v(-80.64, -9.22) * mm, "end": v(-80.47, -9.65) * mm});
            skLineSegment(sketch, "E297", {"start": v(-80.47, -9.65) * mm, "end": v(-80.29, -9.88) * mm});
            skLineSegment(sketch, "E298", {"start": v(-80.29, -9.88) * mm, "end": v(-80.08, -10) * mm});
            skLineSegment(sketch, "E299", {"start": v(-80.08, -10) * mm, "end": v(-79.76, -9.9) * mm});
            skLineSegment(sketch, "E300", {"start": v(-79.76, -9.9) * mm, "end": v(-79.6, -9.68) * mm});
            skLineSegment(sketch, "E301", {"start": v(-79.6, -9.68) * mm, "end": v(-79.55, -9.36) * mm});
            skLineSegment(sketch, "E302", {"start": v(-79.55, -9.36) * mm, "end": v(-79.77, -8.97) * mm});
            skLineSegment(sketch, "E303", {"start": v(-79.77, -8.97) * mm, "end": v(-79.92, -8.75) * mm});
            skLineSegment(sketch, "E304", {"start": v(-79.92, -8.75) * mm, "end": v(-79.92, -8.39) * mm});
            skLineSegment(sketch, "E305", {"start": v(-79.92, -8.39) * mm, "end": v(-79.7, -8.07) * mm});
            skLineSegment(sketch, "E306", {"start": v(-79.7, -8.07) * mm, "end": v(-79.36, -7.95) * mm});
            skLineSegment(sketch, "E307", {"start": v(-79.36, -7.95) * mm, "end": v(-78.94, -8) * mm});
            skLineSegment(sketch, "E308", {"start": v(-78.94, -8) * mm, "end": v(-78.5, -8.2) * mm});
            skLineSegment(sketch, "E309", {"start": v(-78.5, -8.2) * mm, "end": v(-78.05, -8.51) * mm});
            skLineSegment(sketch, "E310", {"start": v(-78.05, -8.51) * mm, "end": v(-77.55, -8.8) * mm});
            skLineSegment(sketch, "E311", {"start": v(-77.55, -8.8) * mm, "end": v(-77.16, -8.85) * mm});
            skLineSegment(sketch, "E312", {"start": v(-77.16, -8.85) * mm, "end": v(-76.84, -8.67) * mm});
            skLineSegment(sketch, "E313", {"start": v(-76.84, -8.67) * mm, "end": v(-76.65, -8.41) * mm});
            skLineSegment(sketch, "E314", {"start": v(-76.65, -8.41) * mm, "end": v(-76.79, -8.04) * mm});
            skLineSegment(sketch, "E315", {"start": v(-76.79, -8.04) * mm, "end": v(-77.26, -7.7) * mm});
            skLineSegment(sketch, "E316", {"start": v(-77.26, -7.7) * mm, "end": v(-78, -7.52) * mm});
            skLineSegment(sketch, "E317", {"start": v(-78, -7.52) * mm, "end": v(-78.63, -7.23) * mm});
            skLineSegment(sketch, "E318", {"start": v(-78.63, -7.23) * mm, "end": v(-79.5, -6.73) * mm});
            skLineSegment(sketch, "E319", {"start": v(-79.5, -6.73) * mm, "end": v(-79.92, -6.22) * mm});
            skLineSegment(sketch, "E320", {"start": v(-79.92, -6.22) * mm, "end": v(-80.13, -5.77) * mm});
            skLineSegment(sketch, "E321", {"start": v(-80.13, -5.77) * mm, "end": v(-80.13, -3.97) * mm});
            skLineSegment(sketch, "E322", {"start": v(-80.13, -3.97) * mm, "end": v(-80.05, -1.3) * mm});
            skLineSegment(sketch, "E323", {"start": v(-80.05, -1.3) * mm, "end": v(-80.05, 2.5) * mm});
            skLineSegment(sketch, "E324", {"start": v(-80.05, 2.5) * mm, "end": v(-80.26, 4.6) * mm});
            skLineSegment(sketch, "E325", {"start": v(-80.26, 4.6) * mm, "end": v(-79.92, 5.31) * mm});
            skLineSegment(sketch, "E326", {"start": v(-79.92, 5.31) * mm, "end": v(-79.54, 5.47) * mm});
            skLineSegment(sketch, "E327", {"start": v(-79.54, 5.47) * mm, "end": v(-78.97, 5.31) * mm});
            skLineSegment(sketch, "E328", {"start": v(-78.97, 5.31) * mm, "end": v(-78.62, 4.8) * mm});
            skLineSegment(sketch, "E329", {"start": v(-78.62, 4.8) * mm, "end": v(-78.5, 4.02) * mm});
            skLineSegment(sketch, "E330", {"start": v(-78.5, 4.02) * mm, "end": v(-78.5, -3.5) * mm});
            skLineSegment(sketch, "E331", {"start": v(-78.5, -3.5) * mm, "end": v(-78.56, -5.14) * mm});
            skLineSegment(sketch, "E332", {"start": v(-78.56, -5.14) * mm, "end": v(-78.38, -5.63) * mm});
            skLineSegment(sketch, "E333", {"start": v(-78.38, -5.63) * mm, "end": v(-77.94, -6.07) * mm});
            skLineSegment(sketch, "E334", {"start": v(-77.94, -6.07) * mm, "end": v(-77, -6.53) * mm});
            skLineSegment(sketch, "E335", {"start": v(-77, -6.53) * mm, "end": v(-76.13, -6.98) * mm});
            skLineSegment(sketch, "E336", {"start": v(-76.13, -6.98) * mm, "end": v(-75.41, -7.67) * mm});
            skLineSegment(sketch, "E337", {"start": v(-75.41, -7.67) * mm, "end": v(-74.9, -8.13) * mm});
            skLineSegment(sketch, "E338", {"start": v(-74.9, -8.13) * mm, "end": v(-74.36, -8.83) * mm});
            skLineSegment(sketch, "E339", {"start": v(-74.36, -8.83) * mm, "end": v(-74.4, -9.35) * mm});
            skLineSegment(sketch, "E340", {"start": v(-74.4, -9.35) * mm, "end": v(-74.82, -9.75) * mm});
            skLineSegment(sketch, "E341", {"start": v(-74.82, -9.75) * mm, "end": v(-75.41, -9.97) * mm});
            skLineSegment(sketch, "E342", {"start": v(-75.41, -9.97) * mm, "end": v(-76.16, -9.95) * mm});
            skLineSegment(sketch, "E343", {"start": v(-76.16, -9.95) * mm, "end": v(-76.9, -9.92) * mm});
            skLineSegment(sketch, "E344", {"start": v(-76.9, -9.92) * mm, "end": v(-77.4, -9.91) * mm});
            skLineSegment(sketch, "E345", {"start": v(-77.4, -9.91) * mm, "end": v(-78, -10.13) * mm});
            skLineSegment(sketch, "E346", {"start": v(-78, -10.13) * mm, "end": v(-78.37, -10.44) * mm});
            skLineSegment(sketch, "E347", {"start": v(-78.37, -10.44) * mm, "end": v(-78.37, -10.96) * mm});
            skLineSegment(sketch, "E348", {"start": v(-78.37, -10.96) * mm, "end": v(-78.53, -11.52) * mm});
            skLineSegment(sketch, "E349", {"start": v(-78.53, -11.52) * mm, "end": v(-79, -11.85) * mm});
            skLineSegment(sketch, "E350", {"start": v(-79, -11.85) * mm, "end": v(-79.74, -12.13) * mm});
            skLineSegment(sketch, "E351", {"start": v(-79.74, -12.13) * mm, "end": v(-80.48, -11.92) * mm});
            skLineSegment(sketch, "E352", {"start": v(-80.48, -11.92) * mm, "end": v(-81.03, -11.48) * mm});
            skLineSegment(sketch, "E353", {"start": v(-81.03, -11.48) * mm, "end": v(-81.28, -11.35) * mm});
            skLineSegment(sketch, "E354", {"start": v(-81.28, -11.35) * mm, "end": v(-81.62, -11.45) * mm});
            skLineSegment(sketch, "E355", {"start": v(-81.62, -11.45) * mm, "end": v(-82.26, -11.75) * mm});
            skLineSegment(sketch, "E356", {"start": v(-82.26, -11.75) * mm, "end": v(-82.76, -11.83) * mm});
            skLineSegment(sketch, "E357", {"start": v(-82.76, -11.83) * mm, "end": v(-83.27, -11.7) * mm});
            skLineSegment(sketch, "E358", {"start": v(-83.27, -11.7) * mm, "end": v(-83.81, -11.23) * mm});
            skLineSegment(sketch, "E359", {"start": v(-83.81, -11.23) * mm, "end": v(-84.15, -10.55) * mm});
            skLineSegment(sketch, "E360", {"start": v(-84.15, -10.55) * mm, "end": v(-84.4, -9.82) * mm});
            skLineSegment(sketch, "E361", {"start": v(-84.4, -9.82) * mm, "end": v(-84.3, -9.2) * mm});
            skLineSegment(sketch, "E362", {"start": v(-84.3, -9.2) * mm, "end": v(-84.15, -8.79) * mm});
            skLineSegment(sketch, "E363", {"start": v(-84.15, -8.79) * mm, "end": v(-83.16, -7.45) * mm});
            skLineSegment(sketch, "E364", {"start": v(-83.16, -7.45) * mm, "end": v(-82.55, -6.42) * mm});
            skLineSegment(sketch, "E365", {"start": v(-82.55, -6.42) * mm, "end": v(-82.4, -5.67) * mm});
            skLineSegment(sketch, "E366", {"start": v(-82.4, -5.67) * mm, "end": v(-82.64, -4) * mm});
            skLineSegment(sketch, "E367", {"start": v(-82.64, -4) * mm, "end": v(-82.64, -2.1) * mm});
            skLineSegment(sketch, "E368", {"start": v(-82.64, -2.1) * mm, "end": v(-82.64, 0.63) * mm});
            skLineSegment(sketch, "E369", {"start": v(-82.64, 0.63) * mm, "end": v(-82.64, 3.66) * mm});
            skLineSegment(sketch, "E370", {"start": v(-82.64, 3.66) * mm, "end": v(-82.74, 4.26) * mm});
            skLineSegment(sketch, "E371", {"start": v(-82.74, 4.26) * mm, "end": v(-82.77, 4.92) * mm});
            skLineSegment(sketch, "E372", {"start": v(-82.77, 4.92) * mm, "end": v(-82.48, 5.34) * mm});
            skLineSegment(sketch, "E373", {"start": v(-82.48, 5.34) * mm, "end": v(-82.06, 5.4) * mm});
            skLineSegment(sketch, "E374", {"start": v(-82.06, 5.4) * mm, "end": v(-81.7, 5.21) * mm});
            skLineSegment(sketch, "E375", {"start": v(-81.7, 5.21) * mm, "end": v(-81.4, 4.82) * mm});
            skLineSegment(sketch, "E376", {"start": v(-81.4, 4.82) * mm, "end": v(-81.15, 4.1) * mm});
            skLineSegment(sketch, "E377", {"start": v(-87.15, -25.3) * mm, "end": v(-86, -21.52) * mm});
            skLineSegment(sketch, "E378", {"start": v(-86, -21.52) * mm, "end": v(-85.26, -19.64) * mm});
            skLineSegment(sketch, "E379", {"start": v(-85.26, -19.64) * mm, "end": v(-84.99, -19.26) * mm});
            skLineSegment(sketch, "E380", {"start": v(-84.99, -19.26) * mm, "end": v(-84.64, -19.08) * mm});
            skLineSegment(sketch, "E381", {"start": v(-84.64, -19.08) * mm, "end": v(-84.4, -19.16) * mm});
            skLineSegment(sketch, "E382", {"start": v(-84.4, -19.16) * mm, "end": v(-84.24, -19.45) * mm});
            skLineSegment(sketch, "E383", {"start": v(-84.24, -19.45) * mm, "end": v(-84.24, -19.86) * mm});
            skLineSegment(sketch, "E384", {"start": v(-84.24, -19.86) * mm, "end": v(-86.07, -25.52) * mm});
            skLineSegment(sketch, "E385", {"start": v(-86.07, -25.52) * mm, "end": v(-86.56, -26.67) * mm});
            skLineSegment(sketch, "E386", {"start": v(-86.56, -26.67) * mm, "end": v(-87.33, -27.6) * mm});
            skLineSegment(sketch, "E387", {"start": v(-87.33, -27.6) * mm, "end": v(-87.94, -27.8) * mm});
            skLineSegment(sketch, "E388", {"start": v(-87.94, -27.8) * mm, "end": v(-88.75, -27.52) * mm});
            skLineSegment(sketch, "E389", {"start": v(-88.75, -27.52) * mm, "end": v(-90.36, -26.2) * mm});
            skLineSegment(sketch, "E390", {"start": v(-90.36, -26.2) * mm, "end": v(-92.02, -24.4) * mm});
            skLineSegment(sketch, "E391", {"start": v(-92.02, -24.4) * mm, "end": v(-92.02, -23.87) * mm});
            skLineSegment(sketch, "E392", {"start": v(-92.02, -23.87) * mm, "end": v(-91.88, -23.47) * mm});
            skLineSegment(sketch, "E393", {"start": v(-91.88, -23.47) * mm, "end": v(-91.63, -23.34) * mm});
            skLineSegment(sketch, "E394", {"start": v(-91.63, -23.34) * mm, "end": v(-91.33, -23.47) * mm});
            skLineSegment(sketch, "E395", {"start": v(-91.33, -23.47) * mm, "end": v(-90.88, -23.91) * mm});
            skLineSegment(sketch, "E396", {"start": v(-90.88, -23.91) * mm, "end": v(-89.75, -24.8) * mm});
            skLineSegment(sketch, "E397", {"start": v(-89.75, -24.8) * mm, "end": v(-88.83, -25.73) * mm});
            skLineSegment(sketch, "E398", {"start": v(-88.83, -25.73) * mm, "end": v(-88.3, -25.98) * mm});
            skLineSegment(sketch, "E399", {"start": v(-88.3, -25.98) * mm, "end": v(-87.72, -25.87) * mm});
            skLineSegment(sketch, "E400", {"start": v(-87.72, -25.87) * mm, "end": v(-87.36, -25.64) * mm});
            skLineSegment(sketch, "E401", {"start": v(-87.36, -25.64) * mm, "end": v(-87.15, -25.3) * mm});
            skLineSegment(sketch, "E402", {"start": v(-84.84, 20.27) * mm, "end": v(-82.7, 21.08) * mm});
            skLineSegment(sketch, "E403", {"start": v(-82.7, 21.08) * mm, "end": v(-81.14, 21.08) * mm});
            skLineSegment(sketch, "E404", {"start": v(-81.14, 21.08) * mm, "end": v(-79.78, 20.7) * mm});
            skLineSegment(sketch, "E405", {"start": v(-79.78, 20.7) * mm, "end": v(-78.91, 20.01) * mm});
            skLineSegment(sketch, "E406", {"start": v(-78.91, 20.01) * mm, "end": v(-78.2, 19) * mm});
            skLineSegment(sketch, "E407", {"start": v(-78.2, 19) * mm, "end": v(-77.85, 17.86) * mm});
            skLineSegment(sketch, "E408", {"start": v(-77.85, 17.86) * mm, "end": v(-77.85, 16.98) * mm});
            skLineSegment(sketch, "E409", {"start": v(-77.85, 16.98) * mm, "end": v(-78.2, 15.89) * mm});
            skLineSegment(sketch, "E410", {"start": v(-78.2, 15.89) * mm, "end": v(-78.96, 14.97) * mm});
            skLineSegment(sketch, "E411", {"start": v(-78.96, 14.97) * mm, "end": v(-79.75, 14.35) * mm});
            skLineSegment(sketch, "E412", {"start": v(-79.75, 14.35) * mm, "end": v(-81.2, 13.89) * mm});
            skLineSegment(sketch, "E413", {"start": v(-81.2, 13.89) * mm, "end": v(-83.05, 13.6) * mm});
            skLineSegment(sketch, "E414", {"start": v(-83.05, 13.6) * mm, "end": v(-84.5, 13.6) * mm});
            skLineSegment(sketch, "E415", {"start": v(-84.5, 13.6) * mm, "end": v(-85.81, 14.35) * mm});
            skLineSegment(sketch, "E416", {"start": v(-85.81, 14.35) * mm, "end": v(-86.8, 15.44) * mm});
            skLineSegment(sketch, "E417", {"start": v(-86.8, 15.44) * mm, "end": v(-87.4, 16.75) * mm});
            skLineSegment(sketch, "E418", {"start": v(-87.4, 16.75) * mm, "end": v(-87.24, 17.91) * mm});
            skLineSegment(sketch, "E419", {"start": v(-87.24, 17.91) * mm, "end": v(-86.2, 19.32) * mm});
            skLineSegment(sketch, "E420", {"start": v(-86.2, 19.32) * mm, "end": v(-84.84, 20.27) * mm});
            skLineSegment(sketch, "E421", {"start": v(-84.32, 14.97) * mm, "end": v(-83.38, 14.8) * mm});
            skLineSegment(sketch, "E422", {"start": v(-83.38, 14.8) * mm, "end": v(-81.04, 15.41) * mm});
            skLineSegment(sketch, "E423", {"start": v(-81.04, 15.41) * mm, "end": v(-79.9, 16.13) * mm});
            skLineSegment(sketch, "E424", {"start": v(-79.9, 16.13) * mm, "end": v(-79.37, 16.76) * mm});
            skLineSegment(sketch, "E425", {"start": v(-79.37, 16.76) * mm, "end": v(-79.03, 17.73) * mm});
            skLineSegment(sketch, "E426", {"start": v(-79.03, 17.73) * mm, "end": v(-79.57, 18.72) * mm});
            skLineSegment(sketch, "E427", {"start": v(-79.57, 18.72) * mm, "end": v(-80.24, 19.52) * mm});
            skLineSegment(sketch, "E428", {"start": v(-80.24, 19.52) * mm, "end": v(-80.6, 19.52) * mm});
            skLineSegment(sketch, "E429", {"start": v(-80.6, 19.52) * mm, "end": v(-81.04, 18.25) * mm});
            skLineSegment(sketch, "E430", {"start": v(-81.04, 18.25) * mm, "end": v(-82.36, 16.53) * mm});
            skLineSegment(sketch, "E431", {"start": v(-82.36, 16.53) * mm, "end": v(-82.82, 16.1) * mm});
            skLineSegment(sketch, "E432", {"start": v(-82.82, 16.1) * mm, "end": v(-83.86, 15.96) * mm});
            skLineSegment(sketch, "E433", {"start": v(-83.86, 15.96) * mm, "end": v(-84.6, 16.05) * mm});
            skLineSegment(sketch, "E434", {"start": v(-84.6, 16.05) * mm, "end": v(-85.07, 16.05) * mm});
            skLineSegment(sketch, "E435", {"start": v(-85.07, 16.05) * mm, "end": v(-85.35, 15.83) * mm});
            skLineSegment(sketch, "E436", {"start": v(-94.85, 16.1) * mm, "end": v(-93.3, 16.87) * mm});
            skLineSegment(sketch, "E437", {"start": v(-93.3, 16.87) * mm, "end": v(-92.45, 17.77) * mm});
            skLineSegment(sketch, "E438", {"start": v(-92.45, 17.77) * mm, "end": v(-92.36, 18.63) * mm});
            skLineSegment(sketch, "E439", {"start": v(-92.36, 18.63) * mm, "end": v(-93, 19.5) * mm});
            skLineSegment(sketch, "E440", {"start": v(-93, 19.5) * mm, "end": v(-93.81, 19.87) * mm});
            skLineSegment(sketch, "E441", {"start": v(-93.81, 19.87) * mm, "end": v(-93.99, 19.71) * mm});
            skLineSegment(sketch, "E442", {"start": v(-93.99, 19.71) * mm, "end": v(-93.99, 18.9) * mm});
            skLineSegment(sketch, "E443", {"start": v(-93.99, 18.9) * mm, "end": v(-94.28, 18.11) * mm});
            skLineSegment(sketch, "E444", {"start": v(-94.28, 18.11) * mm, "end": v(-95.25, 17.1) * mm});
            skLineSegment(sketch, "E445", {"start": v(-95.25, 17.1) * mm, "end": v(-95.9, 16.76) * mm});
            skLineSegment(sketch, "E446", {"start": v(-95.9, 16.76) * mm, "end": v(-96.5, 16.63) * mm});
            skLineSegment(sketch, "E447", {"start": v(-96.5, 16.63) * mm, "end": v(-96.58, 16.47) * mm});
            skLineSegment(sketch, "E448", {"start": v(-96.58, 16.47) * mm, "end": v(-96.5, 16.3) * mm});
            skLineSegment(sketch, "E449", {"start": v(-96.5, 16.3) * mm, "end": v(-95.71, 16.1) * mm});
            skLineSegment(sketch, "E450", {"start": v(-95.71, 16.1) * mm, "end": v(-94.85, 16.1) * mm});
            skEllipse(sketch, "E451", {"center": v(-71.03, -2.22) * mm, "majorRadius": 0.8 * mm, "minorRadius": 0.43 * mm, "majorAxis": v(0.98, -0.18)});
            skEllipse(sketch, "E452", {"center": v(-65.64, -7.04) * mm, "majorRadius": 0.83 * mm, "minorRadius": 0.6 * mm, "majorAxis": v(-0.84, -0.54)});
            skEllipse(sketch, "E453", {"center": v(-66.18, -10.03) * mm, "majorRadius": 0.6 * mm, "minorRadius": 0.44 * mm, "majorAxis": v(-0.97, 0.26)});
            skEllipse(sketch, "E454", {"center": v(-67.18, -12.36) * mm, "majorRadius": 0.95 * mm, "minorRadius": 0.54 * mm, "majorAxis": v(0.97, -0.24)});
            skEllipse(sketch, "E455", {"center": v(-55.9, 2.44) * mm, "majorRadius": 0.67 * mm, "minorRadius": 0.63 * mm, "majorAxis": v(1, -0.13)});
            skLineSegment(sketch, "E456", {"start": v(-87.18, -18.24) * mm, "end": v(-92.08, -15.61) * mm});
            skLineSegment(sketch, "E457", {"start": v(-92.08, -15.61) * mm, "end": v(-95.59, -11.77) * mm});
            skLineSegment(sketch, "E458", {"start": v(-95.59, -11.77) * mm, "end": v(-98.99, -4.88) * mm});
            skLineSegment(sketch, "E459", {"start": v(-98.99, -4.88) * mm, "end": v(-100.28, 0.67) * mm});
            skLineSegment(sketch, "E460", {"start": v(-100.28, 0.67) * mm, "end": v(-100.54, 6.95) * mm});
            skLineSegment(sketch, "E461", {"start": v(-100.54, 6.95) * mm, "end": v(-100.21, 11.18) * mm});
            skLineSegment(sketch, "E462", {"start": v(-100.21, 11.18) * mm, "end": v(-99.65, 15) * mm});
            skLineSegment(sketch, "E463", {"start": v(-99.65, 15) * mm, "end": v(-99.46, 15.57) * mm});
            skLineSegment(sketch, "E464", {"start": v(-99.46, 15.57) * mm, "end": v(-99.59, 16.14) * mm});
            skLineSegment(sketch, "E465", {"start": v(-99.59, 16.14) * mm, "end": v(-99.81, 16.85) * mm});
            skLineSegment(sketch, "E466", {"start": v(-99.81, 16.85) * mm, "end": v(-99.84, 17.57) * mm});
            skLineSegment(sketch, "E467", {"start": v(-99.84, 17.57) * mm, "end": v(-99.72, 18.38) * mm});
            skLineSegment(sketch, "E468", {"start": v(-99.72, 18.38) * mm, "end": v(-99.35, 19.35) * mm});
            skLineSegment(sketch, "E469", {"start": v(-99.35, 19.35) * mm, "end": v(-98.83, 20.04) * mm});
            skLineSegment(sketch, "E470", {"start": v(-98.83, 20.04) * mm, "end": v(-98.13, 20.5) * mm});
            skLineSegment(sketch, "E471", {"start": v(-98.13, 20.5) * mm, "end": v(-97.5, 20.83) * mm});
            skLineSegment(sketch, "E472", {"start": v(-97.5, 20.83) * mm, "end": v(-96.94, 21.34) * mm});
            skLineSegment(sketch, "E473", {"start": v(-96.94, 21.34) * mm, "end": v(-95.59, 23.19) * mm});
            skLineSegment(sketch, "E474", {"start": v(-95.59, 23.19) * mm, "end": v(-94.17, 24.78) * mm});
            skLineSegment(sketch, "E475", {"start": v(-94.17, 24.78) * mm, "end": v(-92.27, 26.51) * mm});
            skLineSegment(sketch, "E476", {"start": v(-92.27, 26.51) * mm, "end": v(-89.8, 27.96) * mm});
            skLineSegment(sketch, "E477", {"start": v(-89.8, 27.96) * mm, "end": v(-88.14, 28.72) * mm});
            skLineSegment(sketch, "E478", {"start": v(-88.14, 28.72) * mm, "end": v(-86.19, 29.21) * mm});
            skLineSegment(sketch, "E479", {"start": v(-86.19, 29.21) * mm, "end": v(-84.45, 29.28) * mm});
            skLineSegment(sketch, "E480", {"start": v(-84.45, 29.28) * mm, "end": v(-81.96, 29.04) * mm});
            skLineSegment(sketch, "E481", {"start": v(-81.96, 29.04) * mm, "end": v(-80.29, 28.72) * mm});
            skLineSegment(sketch, "E482", {"start": v(-80.29, 28.72) * mm, "end": v(-78.76, 28.1) * mm});
            skLineSegment(sketch, "E483", {"start": v(-78.76, 28.1) * mm, "end": v(-77.4, 26.92) * mm});
            skLineSegment(sketch, "E484", {"start": v(-77.4, 26.92) * mm, "end": v(-76.04, 25.03) * mm});
            skLineSegment(sketch, "E485", {"start": v(-76.04, 25.03) * mm, "end": v(-74.94, 22.78) * mm});
            skLineSegment(sketch, "E486", {"start": v(-74.94, 22.78) * mm, "end": v(-74.32, 20.49) * mm});
            skLineSegment(sketch, "E487", {"start": v(-74.32, 20.49) * mm, "end": v(-74.17, 19.04) * mm});
            skLineSegment(sketch, "E488", {"start": v(-74.17, 19.04) * mm, "end": v(-74.17, 16.2) * mm});
            skLineSegment(sketch, "E489", {"start": v(-74.17, 16.2) * mm, "end": v(-74.43, 10.16) * mm});
            skLineSegment(sketch, "E490", {"start": v(-74.43, 10.16) * mm, "end": v(-74, 5.17) * mm});
            skLineSegment(sketch, "E491", {"start": v(-74, 5.17) * mm, "end": v(-73.4, 2.42) * mm});
            skLineSegment(sketch, "E492", {"start": v(-73.4, 2.42) * mm, "end": v(-73.2, 1.39) * mm});
            skLineSegment(sketch, "E493", {"start": v(-73.2, 1.39) * mm, "end": v(-72.96, 0.98) * mm});
            skLineSegment(sketch, "E494", {"start": v(-72.96, 0.98) * mm, "end": v(-72.62, 0.85) * mm});
            skLineSegment(sketch, "E495", {"start": v(-72.62, 0.85) * mm, "end": v(-71.99, 1.19) * mm});
            skLineSegment(sketch, "E496", {"start": v(-71.99, 1.19) * mm, "end": v(-70.46, 1.96) * mm});
            skLineSegment(sketch, "E497", {"start": v(-70.46, 1.96) * mm, "end": v(-68.7, 2.4) * mm});
            skLineSegment(sketch, "E498", {"start": v(-68.7, 2.4) * mm, "end": v(-66.52, 2.45) * mm});
            skLineSegment(sketch, "E499", {"start": v(-66.52, 2.45) * mm, "end": v(-64.86, 2.57) * mm});
            skLineSegment(sketch, "E500", {"start": v(-64.86, 2.57) * mm, "end": v(-63.7, 2.3) * mm});
            skLineSegment(sketch, "E501", {"start": v(-63.7, 2.3) * mm, "end": v(-63.13, 2.08) * mm});
            skLineSegment(sketch, "E502", {"start": v(-63.13, 2.08) * mm, "end": v(-62.7, 2.08) * mm});
            skLineSegment(sketch, "E503", {"start": v(-62.7, 2.08) * mm, "end": v(-62.27, 2.4) * mm});
            skLineSegment(sketch, "E504", {"start": v(-62.27, 2.4) * mm, "end": v(-61.4, 3.63) * mm});
            skLineSegment(sketch, "E505", {"start": v(-61.4, 3.63) * mm, "end": v(-60.2, 6.55) * mm});
            skLineSegment(sketch, "E506", {"start": v(-60.2, 6.55) * mm, "end": v(-59.14, 9.06) * mm});
            skLineSegment(sketch, "E507", {"start": v(-59.14, 9.06) * mm, "end": v(-58.2, 11.58) * mm});
            skLineSegment(sketch, "E508", {"start": v(-58.2, 11.58) * mm, "end": v(-57.05, 12.15) * mm});
            skLineSegment(sketch, "E509", {"start": v(-57.05, 12.15) * mm, "end": v(-55.72, 12.37) * mm});
            skLineSegment(sketch, "E510", {"start": v(-55.72, 12.37) * mm, "end": v(-54.2, 11.9) * mm});
            skLineSegment(sketch, "E511", {"start": v(-54.2, 11.9) * mm, "end": v(-52.9, 10.83) * mm});
            skLineSegment(sketch, "E512", {"start": v(-52.9, 10.83) * mm, "end": v(-52.04, 9.58) * mm});
            skLineSegment(sketch, "E513", {"start": v(-52.04, 9.58) * mm, "end": v(-51.52, 7.67) * mm});
            skLineSegment(sketch, "E514", {"start": v(-51.52, 7.67) * mm, "end": v(-51.52, 6.82) * mm});
            skLineSegment(sketch, "E515", {"start": v(-51.52, 6.82) * mm, "end": v(-52.07, 4.97) * mm});
            skLineSegment(sketch, "E516", {"start": v(-52.07, 4.97) * mm, "end": v(-52.41, 3.57) * mm});
            skLineSegment(sketch, "E517", {"start": v(-52.41, 3.57) * mm, "end": v(-52.99, 2.07) * mm});
            skLineSegment(sketch, "E518", {"start": v(-52.99, 2.07) * mm, "end": v(-53.27, 1.32) * mm});
            skLineSegment(sketch, "E519", {"start": v(-53.27, 1.32) * mm, "end": v(-53.77, 0.64) * mm});
            skLineSegment(sketch, "E520", {"start": v(-53.77, 0.64) * mm, "end": v(-54.23, 0.22) * mm});
            skLineSegment(sketch, "E521", {"start": v(-54.23, 0.22) * mm, "end": v(-54.42, 0) * mm});
            skLineSegment(sketch, "E522", {"start": v(-54.42, 0) * mm, "end": v(-54.45, -0.21) * mm});
            skLineSegment(sketch, "E523", {"start": v(-54.45, -0.21) * mm, "end": v(-54.35, -0.4) * mm});
            skLineSegment(sketch, "E524", {"start": v(-54.35, -0.4) * mm, "end": v(-54.06, -0.42) * mm});
            skLineSegment(sketch, "E525", {"start": v(-54.06, -0.42) * mm, "end": v(-53.55, -0.21) * mm});
            skLineSegment(sketch, "E526", {"start": v(-53.55, -0.21) * mm, "end": v(-52.84, 0.18) * mm});
            skLineSegment(sketch, "E527", {"start": v(-52.84, 0.18) * mm, "end": v(-52.34, 0.31) * mm});
            skLineSegment(sketch, "E528", {"start": v(-52.34, 0.31) * mm, "end": v(-51.76, 0.24) * mm});
            skLineSegment(sketch, "E529", {"start": v(-51.76, 0.24) * mm, "end": v(-51.2, -0.06) * mm});
            skLineSegment(sketch, "E530", {"start": v(-51.2, -0.06) * mm, "end": v(-50.6, -0.51) * mm});
            skLineSegment(sketch, "E531", {"start": v(-50.6, -0.51) * mm, "end": v(-49.88, -0.85) * mm});
            skLineSegment(sketch, "E532", {"start": v(-49.88, -0.85) * mm, "end": v(-49.67, -1.14) * mm});
            skLineSegment(sketch, "E533", {"start": v(-49.67, -1.14) * mm, "end": v(-49.7, -1.47) * mm});
            skLineSegment(sketch, "E534", {"start": v(-49.7, -1.47) * mm, "end": v(-50.03, -1.93) * mm});
            skLineSegment(sketch, "E535", {"start": v(-50.03, -1.93) * mm, "end": v(-49.98, -2.18) * mm});
            skLineSegment(sketch, "E536", {"start": v(-49.98, -2.18) * mm, "end": v(-49.71, -2.35) * mm});
            skLineSegment(sketch, "E537", {"start": v(-49.71, -2.35) * mm, "end": v(-48.73, -2.48) * mm});
            skLineSegment(sketch, "E538", {"start": v(-48.73, -2.48) * mm, "end": v(-48.2, -2.66) * mm});
            skLineSegment(sketch, "E539", {"start": v(-48.2, -2.66) * mm, "end": v(-47.94, -2.9) * mm});
            skLineSegment(sketch, "E540", {"start": v(-47.94, -2.9) * mm, "end": v(-47.8, -3.22) * mm});
            skLineSegment(sketch, "E541", {"start": v(-47.8, -3.22) * mm, "end": v(-47.87, -3.45) * mm});
            skLineSegment(sketch, "E542", {"start": v(-47.87, -3.45) * mm, "end": v(-48.21, -3.63) * mm});
            skLineSegment(sketch, "E543", {"start": v(-48.21, -3.63) * mm, "end": v(-48.63, -3.7) * mm});
            skLineSegment(sketch, "E544", {"start": v(-48.63, -3.7) * mm, "end": v(-49.21, -3.62) * mm});
            skLineSegment(sketch, "E545", {"start": v(-49.21, -3.62) * mm, "end": v(-49.55, -3.59) * mm});
            skLineSegment(sketch, "E546", {"start": v(-49.55, -3.59) * mm, "end": v(-49.68, -3.63) * mm});
            skLineSegment(sketch, "E547", {"start": v(-49.68, -3.63) * mm, "end": v(-49.71, -3.75) * mm});
            skLineSegment(sketch, "E548", {"start": v(-49.71, -3.75) * mm, "end": v(-49.62, -3.95) * mm});
            skLineSegment(sketch, "E549", {"start": v(-49.62, -3.95) * mm, "end": v(-49.31, -4.33) * mm});
            skLineSegment(sketch, "E550", {"start": v(-49.31, -4.33) * mm, "end": v(-48.95, -4.8) * mm});
            skLineSegment(sketch, "E551", {"start": v(-48.95, -4.8) * mm, "end": v(-48.63, -5.23) * mm});
            skLineSegment(sketch, "E552", {"start": v(-48.63, -5.23) * mm, "end": v(-48.55, -5.68) * mm});
            skLineSegment(sketch, "E553", {"start": v(-48.55, -5.68) * mm, "end": v(-48.47, -6.28) * mm});
            skLineSegment(sketch, "E554", {"start": v(-48.47, -6.28) * mm, "end": v(-48.47, -6.75) * mm});
            skLineSegment(sketch, "E555", {"start": v(-48.47, -6.75) * mm, "end": v(-48.62, -7.34) * mm});
            skLineSegment(sketch, "E556", {"start": v(-48.62, -7.34) * mm, "end": v(-49.02, -7.76) * mm});
            skLineSegment(sketch, "E557", {"start": v(-49.02, -7.76) * mm, "end": v(-49.09, -7.96) * mm});
            skLineSegment(sketch, "E558", {"start": v(-49.09, -7.96) * mm, "end": v(-49.03, -8.16) * mm});
            skLineSegment(sketch, "E559", {"start": v(-49.03, -8.16) * mm, "end": v(-48.96, -8.47) * mm});
            skLineSegment(sketch, "E560", {"start": v(-48.96, -8.47) * mm, "end": v(-49.04, -8.65) * mm});
            skLineSegment(sketch, "E561", {"start": v(-49.04, -8.65) * mm, "end": v(-49.27, -8.83) * mm});
            skLineSegment(sketch, "E562", {"start": v(-49.27, -8.83) * mm, "end": v(-49.62, -8.9) * mm});
            skLineSegment(sketch, "E563", {"start": v(-49.62, -8.9) * mm, "end": v(-50.25, -8.96) * mm});
            skLineSegment(sketch, "E564", {"start": v(-50.25, -8.96) * mm, "end": v(-50.74, -9.07) * mm});
            skLineSegment(sketch, "E565", {"start": v(-50.74, -9.07) * mm, "end": v(-50.9, -9.14) * mm});
            skLineSegment(sketch, "E566", {"start": v(-50.9, -9.14) * mm, "end": v(-51.01, -9.3) * mm});
            skLineSegment(sketch, "E567", {"start": v(-51.01, -9.3) * mm, "end": v(-51.01, -9.54) * mm});
            skLineSegment(sketch, "E568", {"start": v(-51.01, -9.54) * mm, "end": v(-51.12, -9.83) * mm});
            skLineSegment(sketch, "E569", {"start": v(-51.12, -9.83) * mm, "end": v(-51.24, -9.99) * mm});
            skLineSegment(sketch, "E570", {"start": v(-51.24, -9.99) * mm, "end": v(-51.52, -10.16) * mm});
            skLineSegment(sketch, "E571", {"start": v(-51.52, -10.16) * mm, "end": v(-51.8, -10.24) * mm});
            skLineSegment(sketch, "E572", {"start": v(-51.8, -10.24) * mm, "end": v(-52.02, -10.2) * mm});
            skLineSegment(sketch, "E573", {"start": v(-52.02, -10.2) * mm, "end": v(-52.23, -10.03) * mm});
            skLineSegment(sketch, "E574", {"start": v(-52.23, -10.03) * mm, "end": v(-52.36, -9.73) * mm});
            skLineSegment(sketch, "E575", {"start": v(-52.36, -9.73) * mm, "end": v(-52.41, -9.48) * mm});
            skLineSegment(sketch, "E576", {"start": v(-52.41, -9.48) * mm, "end": v(-52.5, -9.3) * mm});
            skLineSegment(sketch, "E577", {"start": v(-52.5, -9.3) * mm, "end": v(-52.66, -9.3) * mm});
            skLineSegment(sketch, "E578", {"start": v(-52.66, -9.3) * mm, "end": v(-52.91, -9.36) * mm});
            skLineSegment(sketch, "E579", {"start": v(-52.91, -9.36) * mm, "end": v(-53.16, -9.44) * mm});
            skLineSegment(sketch, "E580", {"start": v(-53.16, -9.44) * mm, "end": v(-53.34, -9.45) * mm});
            skLineSegment(sketch, "E581", {"start": v(-53.34, -9.45) * mm, "end": v(-53.53, -9.35) * mm});
            skLineSegment(sketch, "E582", {"start": v(-53.53, -9.35) * mm, "end": v(-53.73, -9.2) * mm});
            skLineSegment(sketch, "E583", {"start": v(-53.73, -9.2) * mm, "end": v(-53.91, -9.16) * mm});
            skLineSegment(sketch, "E584", {"start": v(-53.91, -9.16) * mm, "end": v(-54.07, -9.17) * mm});
            skLineSegment(sketch, "E585", {"start": v(-54.07, -9.17) * mm, "end": v(-54.23, -9.3) * mm});
            skLineSegment(sketch, "E586", {"start": v(-54.23, -9.3) * mm, "end": v(-54.45, -9.52) * mm});
            skLineSegment(sketch, "E587", {"start": v(-54.45, -9.52) * mm, "end": v(-54.52, -9.91) * mm});
            skLineSegment(sketch, "E588", {"start": v(-54.52, -9.91) * mm, "end": v(-54.52, -10.51) * mm});
            skLineSegment(sketch, "E589", {"start": v(-54.52, -10.51) * mm, "end": v(-54.52, -10.9) * mm});
            skLineSegment(sketch, "E590", {"start": v(-54.52, -10.9) * mm, "end": v(-54.65, -11.3) * mm});
            skLineSegment(sketch, "E591", {"start": v(-54.65, -11.3) * mm, "end": v(-55.46, -12.6) * mm});
            skLineSegment(sketch, "E592", {"start": v(-55.46, -12.6) * mm, "end": v(-57.3, -15.04) * mm});
            skLineSegment(sketch, "E593", {"start": v(-57.3, -15.04) * mm, "end": v(-59.48, -16.94) * mm});
            skLineSegment(sketch, "E594", {"start": v(-59.48, -16.94) * mm, "end": v(-61.95, -18.5) * mm});
            skLineSegment(sketch, "E595", {"start": v(-61.95, -18.5) * mm, "end": v(-64.87, -19.36) * mm});
            skLineSegment(sketch, "E596", {"start": v(-64.87, -19.36) * mm, "end": v(-66.8, -19.36) * mm});
            skLineSegment(sketch, "E597", {"start": v(-66.8, -19.36) * mm, "end": v(-67.31, -19.45) * mm});
            skLineSegment(sketch, "E598", {"start": v(-67.31, -19.45) * mm, "end": v(-67.5, -19.6) * mm});
            skLineSegment(sketch, "E599", {"start": v(-67.5, -19.6) * mm, "end": v(-67.57, -19.89) * mm});
            skLineSegment(sketch, "E600", {"start": v(-67.57, -19.89) * mm, "end": v(-67.88, -22.38) * mm});
            skLineSegment(sketch, "E601", {"start": v(-67.88, -22.38) * mm, "end": v(-68.02, -23.2) * mm});
            skLineSegment(sketch, "E602", {"start": v(-68.02, -23.2) * mm, "end": v(-67.75, -25.09) * mm});
            skLineSegment(sketch, "E603", {"start": v(-67.75, -25.09) * mm, "end": v(-67.93, -26.5) * mm});
            skLineSegment(sketch, "E604", {"start": v(-67.93, -26.5) * mm, "end": v(-68.06, -28.17) * mm});
            skLineSegment(sketch, "E605", {"start": v(-68.06, -28.17) * mm, "end": v(-68.54, -28.72) * mm});
            skLineSegment(sketch, "E606", {"start": v(-68.54, -28.72) * mm, "end": v(-69.36, -29.07) * mm});
            skLineSegment(sketch, "E607", {"start": v(-69.36, -29.07) * mm, "end": v(-70.14, -29.05) * mm});
            skLineSegment(sketch, "E608", {"start": v(-70.14, -29.05) * mm, "end": v(-71.47, -28.48) * mm});
            skLineSegment(sketch, "E609", {"start": v(-71.47, -28.48) * mm, "end": v(-73.37, -27.35) * mm});
            skLineSegment(sketch, "E610", {"start": v(-73.37, -27.35) * mm, "end": v(-74.74, -26.57) * mm});
            skLineSegment(sketch, "E611", {"start": v(-74.74, -26.57) * mm, "end": v(-76.24, -25.09) * mm});
            skLineSegment(sketch, "E612", {"start": v(-76.24, -25.09) * mm, "end": v(-77.3, -23.53) * mm});
            skLineSegment(sketch, "E613", {"start": v(-77.3, -23.53) * mm, "end": v(-77.8, -22.58) * mm});
            skLineSegment(sketch, "E614", {"start": v(-77.8, -22.58) * mm, "end": v(-77.76, -21.9) * mm});
            skLineSegment(sketch, "E615", {"start": v(-77.76, -21.9) * mm, "end": v(-77.34, -21.38) * mm});
            skLineSegment(sketch, "E616", {"start": v(-77.34, -21.38) * mm, "end": v(-76.86, -21.14) * mm});
            skLineSegment(sketch, "E617", {"start": v(-76.86, -21.14) * mm, "end": v(-76.4, -21) * mm});
            skLineSegment(sketch, "E618", {"start": v(-76.4, -21) * mm, "end": v(-75.39, -21.08) * mm});
            skLineSegment(sketch, "E619", {"start": v(-75.39, -21.08) * mm, "end": v(-74.54, -21.26) * mm});
            skLineSegment(sketch, "E620", {"start": v(-74.54, -21.26) * mm, "end": v(-73.65, -21.73) * mm});
            skLineSegment(sketch, "E621", {"start": v(-73.65, -21.73) * mm, "end": v(-73.36, -21.87) * mm});
            skLineSegment(sketch, "E622", {"start": v(-73.36, -21.87) * mm, "end": v(-73, -21.83) * mm});
            skLineSegment(sketch, "E623", {"start": v(-73, -21.83) * mm, "end": v(-72.78, -21.65) * mm});
            skLineSegment(sketch, "E624", {"start": v(-72.78, -21.65) * mm, "end": v(-72.67, -21.48) * mm});
            skLineSegment(sketch, "E625", {"start": v(-72.67, -21.48) * mm, "end": v(-72.6, -20.78) * mm});
            skLineSegment(sketch, "E626", {"start": v(-72.6, -20.78) * mm, "end": v(-72.6, -20.3) * mm});
            skLineSegment(sketch, "E627", {"start": v(-72.6, -20.3) * mm, "end": v(-72.84, -19.96) * mm});
            skLineSegment(sketch, "E628", {"start": v(-72.84, -19.96) * mm, "end": v(-73.16, -19.75) * mm});
            skLineSegment(sketch, "E629", {"start": v(-73.16, -19.75) * mm, "end": v(-73.63, -19.8) * mm});
            skLineSegment(sketch, "E630", {"start": v(-73.63, -19.8) * mm, "end": v(-74.44, -20) * mm});
            skLineSegment(sketch, "E631", {"start": v(-74.44, -20) * mm, "end": v(-75.74, -20.25) * mm});
            skLineSegment(sketch, "E632", {"start": v(-75.74, -20.25) * mm, "end": v(-77.5, -20.28) * mm});
            skLineSegment(sketch, "E633", {"start": v(-77.5, -20.28) * mm, "end": v(-79.06, -20.19) * mm});
            skLineSegment(sketch, "E634", {"start": v(-79.06, -20.19) * mm, "end": v(-80.89, -20.03) * mm});
            skLineSegment(sketch, "E635", {"start": v(-80.89, -20.03) * mm, "end": v(-82.17, -19.77) * mm});
            skLineSegment(sketch, "E636", {"start": v(-82.17, -19.77) * mm, "end": v(-82.4, -19.85) * mm});
            skLineSegment(sketch, "E637", {"start": v(-82.4, -19.85) * mm, "end": v(-82.59, -20.1) * mm});
            skLineSegment(sketch, "E638", {"start": v(-82.59, -20.1) * mm, "end": v(-82.77, -20.93) * mm});
            skLineSegment(sketch, "E639", {"start": v(-82.77, -20.93) * mm, "end": v(-83.16, -22.4) * mm});
            skLineSegment(sketch, "E640", {"start": v(-83.16, -22.4) * mm, "end": v(-83.65, -23.75) * mm});
            skLineSegment(sketch, "E641", {"start": v(-83.65, -23.75) * mm, "end": v(-84.37, -25.08) * mm});
            skLineSegment(sketch, "E642", {"start": v(-84.37, -25.08) * mm, "end": v(-85.4, -27.63) * mm});
            skLineSegment(sketch, "E643", {"start": v(-85.4, -27.63) * mm, "end": v(-85.7, -28.23) * mm});
            skLineSegment(sketch, "E644", {"start": v(-85.7, -28.23) * mm, "end": v(-86.57, -29.25) * mm});
            skLineSegment(sketch, "E645", {"start": v(-86.57, -29.25) * mm, "end": v(-86.84, -29.42) * mm});
            skLineSegment(sketch, "E646", {"start": v(-86.84, -29.42) * mm, "end": v(-87.27, -29.58) * mm});
            skLineSegment(sketch, "E647", {"start": v(-87.27, -29.58) * mm, "end": v(-87.82, -29.57) * mm});
            skLineSegment(sketch, "E648", {"start": v(-87.82, -29.57) * mm, "end": v(-88.24, -29.49) * mm});
            skLineSegment(sketch, "E649", {"start": v(-88.24, -29.49) * mm, "end": v(-89.02, -29.14) * mm});
            skLineSegment(sketch, "E650", {"start": v(-89.02, -29.14) * mm, "end": v(-89.55, -28.84) * mm});
            skLineSegment(sketch, "E651", {"start": v(-89.55, -28.84) * mm, "end": v(-90.81, -27.86) * mm});
            skLineSegment(sketch, "E652", {"start": v(-90.81, -27.86) * mm, "end": v(-92.05, -26.69) * mm});
            skLineSegment(sketch, "E653", {"start": v(-92.05, -26.69) * mm, "end": v(-93.19, -25.17) * mm});
            skLineSegment(sketch, "E654", {"start": v(-93.19, -25.17) * mm, "end": v(-93.8, -24) * mm});
            skLineSegment(sketch, "E655", {"start": v(-93.8, -24) * mm, "end": v(-94.03, -23.23) * mm});
            skLineSegment(sketch, "E656", {"start": v(-94.03, -23.23) * mm, "end": v(-93.96, -22.6) * mm});
            skLineSegment(sketch, "E657", {"start": v(-93.96, -22.6) * mm, "end": v(-93.55, -22.1) * mm});
            skLineSegment(sketch, "E658", {"start": v(-93.55, -22.1) * mm, "end": v(-92.97, -21.88) * mm});
            skLineSegment(sketch, "E659", {"start": v(-92.97, -21.88) * mm, "end": v(-92.14, -21.94) * mm});
            skLineSegment(sketch, "E660", {"start": v(-92.14, -21.94) * mm, "end": v(-91.5, -22.06) * mm});
            skLineSegment(sketch, "E661", {"start": v(-91.5, -22.06) * mm, "end": v(-90.8, -22.34) * mm});
            skLineSegment(sketch, "E662", {"start": v(-90.8, -22.34) * mm, "end": v(-90.12, -22.7) * mm});
            skLineSegment(sketch, "E663", {"start": v(-90.12, -22.7) * mm, "end": v(-89.6, -23.09) * mm});
            skLineSegment(sketch, "E664", {"start": v(-89.6, -23.09) * mm, "end": v(-89.12, -23.52) * mm});
            skLineSegment(sketch, "E665", {"start": v(-89.12, -23.52) * mm, "end": v(-88.78, -23.77) * mm});
            skLineSegment(sketch, "E666", {"start": v(-88.78, -23.77) * mm, "end": v(-88.52, -23.77) * mm});
            skLineSegment(sketch, "E667", {"start": v(-88.52, -23.77) * mm, "end": v(-88.3, -23.61) * mm});
            skLineSegment(sketch, "E668", {"start": v(-88.3, -23.61) * mm, "end": v(-88.14, -23.4) * mm});
            skLineSegment(sketch, "E669", {"start": v(-88.14, -23.4) * mm, "end": v(-88.07, -23.22) * mm});
            skLineSegment(sketch, "E670", {"start": v(-88.07, -23.22) * mm, "end": v(-87.98, -22.63) * mm});
            skLineSegment(sketch, "E671", {"start": v(-87.98, -22.63) * mm, "end": v(-87.9, -21.88) * mm});
            skLineSegment(sketch, "E672", {"start": v(-87.9, -21.88) * mm, "end": v(-87.56, -21.3) * mm});
            skLineSegment(sketch, "E673", {"start": v(-87.56, -21.3) * mm, "end": v(-87.2, -20.9) * mm});
            skLineSegment(sketch, "E674", {"start": v(-87.2, -20.9) * mm, "end": v(-87.11, -20.1) * mm});
            skLineSegment(sketch, "E675", {"start": v(-87.11, -20.1) * mm, "end": v(-86.47, -19.13) * mm});
            skLineSegment(sketch, "E676", {"start": v(-86.47, -19.13) * mm, "end": v(-86.47, -18.94) * mm});
            skLineSegment(sketch, "E677", {"start": v(-86.47, -18.94) * mm, "end": v(-86.61, -18.7) * mm});
            skLineSegment(sketch, "E678", {"start": v(-86.61, -18.7) * mm, "end": v(-86.84, -18.43) * mm});
            skLineSegment(sketch, "E679", {"start": v(-86.84, -18.43) * mm, "end": v(-87.18, -18.24) * mm});
            skLineSegment(sketch, "E680", {"start": v(-61.56, 0.61) * mm, "end": v(-60.45, 1.82) * mm});
            skLineSegment(sketch, "E681", {"start": v(-60.45, 1.82) * mm, "end": v(-58.92, 4.54) * mm});
            skLineSegment(sketch, "E682", {"start": v(-58.92, 4.54) * mm, "end": v(-57.48, 8.28) * mm});
            skLineSegment(sketch, "E683", {"start": v(-57.48, 8.28) * mm, "end": v(-56.86, 10.06) * mm});
            skLineSegment(sketch, "E684", {"start": v(-56.86, 10.06) * mm, "end": v(-56.6, 10.4) * mm});
            skLineSegment(sketch, "E685", {"start": v(-56.6, 10.4) * mm, "end": v(-56.12, 10.66) * mm});
            skLineSegment(sketch, "E686", {"start": v(-56.12, 10.66) * mm, "end": v(-55.48, 10.76) * mm});
            skLineSegment(sketch, "E687", {"start": v(-55.48, 10.76) * mm, "end": v(-55.01, 10.55) * mm});
            skLineSegment(sketch, "E688", {"start": v(-55.01, 10.55) * mm, "end": v(-54.27, 10.05) * mm});
            skLineSegment(sketch, "E689", {"start": v(-54.27, 10.05) * mm, "end": v(-53.75, 9.58) * mm});
            skLineSegment(sketch, "E690", {"start": v(-53.75, 9.58) * mm, "end": v(-53.38, 8.92) * mm});
            skLineSegment(sketch, "E691", {"start": v(-53.38, 8.92) * mm, "end": v(-53.13, 8.1) * mm});
            skLineSegment(sketch, "E692", {"start": v(-53.13, 8.1) * mm, "end": v(-53.05, 7.63) * mm});
            skLineSegment(sketch, "E693", {"start": v(-53.05, 7.63) * mm, "end": v(-53.12, 7.1) * mm});
            skLineSegment(sketch, "E694", {"start": v(-53.12, 7.1) * mm, "end": v(-53.27, 6.58) * mm});
            skLineSegment(sketch, "E695", {"start": v(-53.27, 6.58) * mm, "end": v(-53.5, 4.99) * mm});
            skLineSegment(sketch, "E696", {"start": v(-53.5, 4.99) * mm, "end": v(-53.6, 4.36) * mm});
            skLineSegment(sketch, "E697", {"start": v(-53.6, 4.36) * mm, "end": v(-54.16, 3.16) * mm});
            skLineSegment(sketch, "E698", {"start": v(-54.16, 3.16) * mm, "end": v(-54.5, 2.2) * mm});
            skLineSegment(sketch, "E699", {"start": v(-54.5, 2.2) * mm, "end": v(-54.83, 1.64) * mm});
            skLineSegment(sketch, "E700", {"start": v(-54.83, 1.64) * mm, "end": v(-55.94, 0.6) * mm});
            skLineSegment(sketch, "E701", {"start": v(-55.94, 0.6) * mm, "end": v(-56.64, -0.18) * mm});
            skLineSegment(sketch, "E702", {"start": v(-56.64, -0.18) * mm, "end": v(-57.26, -0.72) * mm});
            skLineSegment(sketch, "E703", {"start": v(-57.26, -0.72) * mm, "end": v(-57.38, -0.93) * mm});
            skLineSegment(sketch, "E704", {"start": v(-57.38, -0.93) * mm, "end": v(-57.4, -1.12) * mm});
            skLineSegment(sketch, "E705", {"start": v(-57.4, -1.12) * mm, "end": v(-57.28, -1.44) * mm});
            skLineSegment(sketch, "E706", {"start": v(-57.28, -1.44) * mm, "end": v(-57.01, -1.75) * mm});
            skLineSegment(sketch, "E707", {"start": v(-57.01, -1.75) * mm, "end": v(-56.8, -1.89) * mm});
            skLineSegment(sketch, "E708", {"start": v(-56.8, -1.89) * mm, "end": v(-56.46, -1.97) * mm});
            skLineSegment(sketch, "E709", {"start": v(-56.46, -1.97) * mm, "end": v(-56.08, -2.04) * mm});
            skLineSegment(sketch, "E710", {"start": v(-56.08, -2.04) * mm, "end": v(-55.6, -2.16) * mm});
            skLineSegment(sketch, "E711", {"start": v(-55.6, -2.16) * mm, "end": v(-55.44, -2.21) * mm});
            skLineSegment(sketch, "E712", {"start": v(-55.44, -2.21) * mm, "end": v(-55.2, -2.12) * mm});
            skLineSegment(sketch, "E713", {"start": v(-55.2, -2.12) * mm, "end": v(-54.64, -1.89) * mm});
            skLineSegment(sketch, "E714", {"start": v(-54.64, -1.89) * mm, "end": v(-54.05, -1.54) * mm});
            skLineSegment(sketch, "E715", {"start": v(-54.05, -1.54) * mm, "end": v(-53.31, -1.29) * mm});
            skLineSegment(sketch, "E716", {"start": v(-53.31, -1.29) * mm, "end": v(-52.88, -1.23) * mm});
            skLineSegment(sketch, "E717", {"start": v(-52.88, -1.23) * mm, "end": v(-52.45, -1.38) * mm});
            skLineSegment(sketch, "E718", {"start": v(-52.45, -1.38) * mm, "end": v(-52.23, -1.47) * mm});
            skLineSegment(sketch, "E719", {"start": v(-52.23, -1.47) * mm, "end": v(-52.14, -1.57) * mm});
            skLineSegment(sketch, "E720", {"start": v(-52.14, -1.57) * mm, "end": v(-52.14, -1.68) * mm});
            skLineSegment(sketch, "E721", {"start": v(-52.14, -1.68) * mm, "end": v(-52.26, -1.82) * mm});
            skLineSegment(sketch, "E722", {"start": v(-52.26, -1.82) * mm, "end": v(-52.22, -2.29) * mm});
            skLineSegment(sketch, "E723", {"start": v(-52.22, -2.29) * mm, "end": v(-52.3, -2.85) * mm});
            skLineSegment(sketch, "E724", {"start": v(-52.3, -2.85) * mm, "end": v(-52.27, -3.28) * mm});
            skLineSegment(sketch, "E725", {"start": v(-52.27, -3.28) * mm, "end": v(-52.29, -3.42) * mm});
            skLineSegment(sketch, "E726", {"start": v(-52.29, -3.42) * mm, "end": v(-52.4, -3.45) * mm});
            skLineSegment(sketch, "E727", {"start": v(-52.4, -3.45) * mm, "end": v(-52.87, -3.38) * mm});
            skLineSegment(sketch, "E728", {"start": v(-52.87, -3.38) * mm, "end": v(-53.55, -2.99) * mm});
            skLineSegment(sketch, "E729", {"start": v(-53.55, -2.99) * mm, "end": v(-53.78, -2.75) * mm});
            skLineSegment(sketch, "E730", {"start": v(-53.78, -2.75) * mm, "end": v(-53.97, -2.63) * mm});
            skLineSegment(sketch, "E731", {"start": v(-53.97, -2.63) * mm, "end": v(-54.15, -2.64) * mm});
            skLineSegment(sketch, "E732", {"start": v(-54.15, -2.64) * mm, "end": v(-54.43, -2.7) * mm});
            skLineSegment(sketch, "E733", {"start": v(-54.43, -2.7) * mm, "end": v(-54.66, -2.83) * mm});
            skLineSegment(sketch, "E734", {"start": v(-54.66, -2.83) * mm, "end": v(-54.88, -3.02) * mm});
            skLineSegment(sketch, "E735", {"start": v(-54.88, -3.02) * mm, "end": v(-54.93, -3.22) * mm});
            skLineSegment(sketch, "E736", {"start": v(-54.93, -3.22) * mm, "end": v(-54.93, -3.35) * mm});
            skLineSegment(sketch, "E737", {"start": v(-54.93, -3.35) * mm, "end": v(-54.86, -3.6) * mm});
            skLineSegment(sketch, "E738", {"start": v(-54.86, -3.6) * mm, "end": v(-54.67, -3.9) * mm});
            skLineSegment(sketch, "E739", {"start": v(-54.67, -3.9) * mm, "end": v(-54.35, -4.2) * mm});
            skLineSegment(sketch, "E740", {"start": v(-54.35, -4.2) * mm, "end": v(-53.75, -4.45) * mm});
            skLineSegment(sketch, "E741", {"start": v(-53.75, -4.45) * mm, "end": v(-53.1, -4.78) * mm});
            skLineSegment(sketch, "E742", {"start": v(-53.1, -4.78) * mm, "end": v(-52.76, -4.89) * mm});
            skLineSegment(sketch, "E743", {"start": v(-52.76, -4.89) * mm, "end": v(-51.3, -5.05) * mm});
            skLineSegment(sketch, "E744", {"start": v(-51.3, -5.05) * mm, "end": v(-50.96, -5.05) * mm});
            skLineSegment(sketch, "E745", {"start": v(-50.96, -5.05) * mm, "end": v(-50.85, -5.12) * mm});
            skLineSegment(sketch, "E746", {"start": v(-50.85, -5.12) * mm, "end": v(-50.45, -5.42) * mm});
            skLineSegment(sketch, "E747", {"start": v(-50.45, -5.42) * mm, "end": v(-50.2, -5.75) * mm});
            skLineSegment(sketch, "E748", {"start": v(-50.2, -5.75) * mm, "end": v(-50.15, -6.07) * mm});
            skLineSegment(sketch, "E749", {"start": v(-50.15, -6.07) * mm, "end": v(-50.17, -6.3) * mm});
            skLineSegment(sketch, "E750", {"start": v(-50.17, -6.3) * mm, "end": v(-50.28, -6.45) * mm});
            skLineSegment(sketch, "E751", {"start": v(-50.28, -6.45) * mm, "end": v(-50.41, -6.57) * mm});
            skLineSegment(sketch, "E752", {"start": v(-50.41, -6.57) * mm, "end": v(-50.6, -6.63) * mm});
            skLineSegment(sketch, "E753", {"start": v(-50.6, -6.63) * mm, "end": v(-50.8, -6.53) * mm});
            skLineSegment(sketch, "E754", {"start": v(-50.8, -6.53) * mm, "end": v(-51.02, -6.47) * mm});
            skLineSegment(sketch, "E755", {"start": v(-51.02, -6.47) * mm, "end": v(-51.23, -6.52) * mm});
            skLineSegment(sketch, "E756", {"start": v(-51.23, -6.52) * mm, "end": v(-51.39, -6.65) * mm});
            skLineSegment(sketch, "E757", {"start": v(-51.39, -6.65) * mm, "end": v(-51.48, -6.82) * mm});
            skLineSegment(sketch, "E758", {"start": v(-51.48, -6.82) * mm, "end": v(-51.5, -7) * mm});
            skLineSegment(sketch, "E759", {"start": v(-51.5, -7) * mm, "end": v(-51.4, -7.26) * mm});
            skLineSegment(sketch, "E760", {"start": v(-51.4, -7.26) * mm, "end": v(-51.36, -7.43) * mm});
            skLineSegment(sketch, "E761", {"start": v(-51.36, -7.43) * mm, "end": v(-51.4, -7.53) * mm});
            skLineSegment(sketch, "E762", {"start": v(-51.4, -7.53) * mm, "end": v(-51.55, -7.55) * mm});
            skLineSegment(sketch, "E763", {"start": v(-51.55, -7.55) * mm, "end": v(-51.73, -7.44) * mm});
            skLineSegment(sketch, "E764", {"start": v(-51.73, -7.44) * mm, "end": v(-51.9, -7.33) * mm});
            skLineSegment(sketch, "E765", {"start": v(-51.9, -7.33) * mm, "end": v(-52.21, -7.33) * mm});
            skLineSegment(sketch, "E766", {"start": v(-52.21, -7.33) * mm, "end": v(-53.44, -7.36) * mm});
            skLineSegment(sketch, "E767", {"start": v(-53.44, -7.36) * mm, "end": v(-53.71, -7.18) * mm});
            skLineSegment(sketch, "E768", {"start": v(-53.71, -7.18) * mm, "end": v(-53.95, -7.05) * mm});
            skLineSegment(sketch, "E769", {"start": v(-53.95, -7.05) * mm, "end": v(-54.56, -6.96) * mm});
            skLineSegment(sketch, "E770", {"start": v(-54.56, -6.96) * mm, "end": v(-54.8, -6.79) * mm});
            skLineSegment(sketch, "E771", {"start": v(-54.8, -6.79) * mm, "end": v(-55.45, -5.56) * mm});
            skLineSegment(sketch, "E772", {"start": v(-55.45, -5.56) * mm, "end": v(-55.9, -4.74) * mm});
            skLineSegment(sketch, "E773", {"start": v(-55.9, -4.74) * mm, "end": v(-56.98, -3.7) * mm});
            skLineSegment(sketch, "E774", {"start": v(-56.98, -3.7) * mm, "end": v(-57.96, -2.97) * mm});
            skLineSegment(sketch, "E775", {"start": v(-57.96, -2.97) * mm, "end": v(-58.62, -2.58) * mm});
            skLineSegment(sketch, "E776", {"start": v(-58.62, -2.58) * mm, "end": v(-59.7, -2.14) * mm});
            skLineSegment(sketch, "E777", {"start": v(-59.7, -2.14) * mm, "end": v(-60.9, -1.75) * mm});
            skLineSegment(sketch, "E778", {"start": v(-60.9, -1.75) * mm, "end": v(-61.4, -1.63) * mm});
            skLineSegment(sketch, "E779", {"start": v(-61.4, -1.63) * mm, "end": v(-61.93, -1.63) * mm});
            skLineSegment(sketch, "E780", {"start": v(-61.93, -1.63) * mm, "end": v(-62.14, -1.56) * mm});
            skLineSegment(sketch, "E781", {"start": v(-62.14, -1.56) * mm, "end": v(-62.3, -1.4) * mm});
            skLineSegment(sketch, "E782", {"start": v(-62.3, -1.4) * mm, "end": v(-62.42, -1.2) * mm});
            skLineSegment(sketch, "E783", {"start": v(-62.42, -1.2) * mm, "end": v(-62.44, -0.95) * mm});
            skLineSegment(sketch, "E784", {"start": v(-62.44, -0.95) * mm, "end": v(-62.4, -0.72) * mm});
            skLineSegment(sketch, "E785", {"start": v(-62.4, -0.72) * mm, "end": v(-62.36, -0.55) * mm});
            skLineSegment(sketch, "E786", {"start": v(-62.36, -0.55) * mm, "end": v(-62.08, -0.1) * mm});
            skLineSegment(sketch, "E787", {"start": v(-62.08, -0.1) * mm, "end": v(-61.83, 0.28) * mm});
            skLineSegment(sketch, "E788", {"start": v(-61.83, 0.28) * mm, "end": v(-61.56, 0.61) * mm});
            skLineSegment(sketch, "E789", {"start": v(-59.52, -14.64) * mm, "end": v(-57.3, -15.04) * mm});
            skLineSegment(sketch, "E790", {"start": v(-84.45, 29.28) * mm, "end": v(-83.35, 27.56) * mm});
            skLineSegment(sketch, "E791", {"start": v(-95.59, -11.77) * mm, "end": v(-93.01, -11.66) * mm});
            skLineSegment(sketch, "E792", {"start": v(-75.18, 2.3) * mm, "end": v(-73.4, 2.42) * mm});
            skLineSegment(sketch, "E793", {"start": v(-58.23, -4.36) * mm, "end": v(-57.96, -2.97) * mm});
            skLineSegment(sketch, "E794", {"start": v(-55.94, 0.6) * mm, "end": v(-53.77, 0.64) * mm});
            skEllipse(sketch, "E795", {"center": v(-54.57, 4.58) * mm, "majorRadius": 0.64 * mm, "minorRadius": 0.55 * mm, "majorAxis": v(0.3, 0.95)});
            skEllipse(sketch, "E796", {"center": v(-65.7, -15.24) * mm, "majorRadius": 0.89 * mm, "minorRadius": 0.55 * mm, "majorAxis": v(1, 0.1)});
            skLineSegment(sketch, "E797", {"start": v(-84.32, 14.97) * mm, "end": v(-85.35, 15.83) * mm});
            skSolve(sketch);
        }
        {
            var Q0;
            Q0=makeQuery(id+"F4.imprint","IMPRINT",FACE,{"disambiguationData":[TD([[makeQuery(id+"F4.imprint","IMPRINT",EDGE,{"derivedFrom":sQuery(id+"F4.wireOp",EDGE,"E454")}),1.0]])]});
            var Q1;
            Q1=makeQuery(id+"F4.imprint","IMPRINT",FACE,{"disambiguationData":[TD([[makeQuery(id+"F4.imprint","IMPRINT",EDGE,{"derivedFrom":sQuery(id+"F4.wireOp",EDGE,"E453")}),1.0]])]});
            var Q2;
            Q2=makeQuery(id+"F4.imprint","IMPRINT",FACE,{"disambiguationData":[TD([[makeQuery(id+"F4.imprint","IMPRINT",EDGE,{"derivedFrom":sQuery(id+"F4.wireOp",EDGE,"E452")}),1.0]])]});
            var Q3;
            Q3=makeQuery(id+"F4.imprint","IMPRINT",FACE,{"disambiguationData":[TD([[makeQuery(id+"F4.imprint","IMPRINT",EDGE,{"derivedFrom":sQuery(id+"F4.wireOp",EDGE,"E451")}),1.0]])]});
            var Q4;
            Q4=makeQuery(id+"F4.imprint","IMPRINT",FACE,{"disambiguationData":[TD([[makeQuery(id+"F4.imprint","IMPRINT",EDGE,{"derivedFrom":sQuery(id+"F4.wireOp",EDGE,"E455")}),1.0]])]});
            var Q5;
            Q5=makeQuery(id+"F4.imprint","IMPRINT",FACE,{"disambiguationData":[TD([[makeQuery(id+"F4.imprint","IMPRINT",EDGE,{"derivedFrom":sQuery(id+"F4.wireOp",EDGE,"E278")}),-1.0]])]});
            extrude(context, id + "F5", {"entities" : qUnion([Q0, Q1, Q2, Q3, Q4, Q5]), "operationType" : NewBodyOperationType.REMOVE, "oppositeDirection" : true, "depth" : 2 * mm});
        }
        {
            var Q0;
            Q0 = qSketchRegion(id + "F4", true);
            extrude(context, id + "F6", {"entities" : qUnion([Q0]), "operationType" : NewBodyOperationType.REMOVE, "oppositeDirection" : true, "depth" : 2 * mm});
        }
        {
            var Q0;
            Q0=makeQuery(id+"F4.imprint","IMPRINT",FACE,{"disambiguationData":[TD([[makeQuery(id+"F4.imprint","IMPRINT",EDGE,{"derivedFrom":sQuery(id+"F4.wireOp",EDGE,"E402")}),-1.0]])]});
            var Q1;
            Q1=sQuery(id+"F4.wireOp",EDGE,"E402");
            extrude(context, id + "F7", {"entities" : qUnion([Q0]), "operationType" : NewBodyOperationType.REMOVE, "surfaceEntities" : qUnion([Q1]), "oppositeDirection" : true, "depth" : 2 * mm});
        }
        {
            var Q0;
            Q0=makeQuery(id+"F4.imprint","IMPRINT",FACE,{"disambiguationData":[TD([[makeQuery(id+"F4.imprint","IMPRINT",EDGE,{"derivedFrom":sQuery(id+"F4.wireOp",EDGE,"E796")}),1.0]])]});
            var Q1;
            Q1=makeQuery(id+"F4.imprint","IMPRINT",FACE,{"disambiguationData":[TD([[makeQuery(id+"F4.imprint","IMPRINT",EDGE,{"derivedFrom":sQuery(id+"F4.wireOp",EDGE,"E795")}),1.0]])]});
            extrude(context, id + "F8", {"entities" : qUnion([Q0, Q1]), "operationType" : NewBodyOperationType.REMOVE, "oppositeDirection" : true, "depth" : 2 * mm});
        }
        {
            var Q0;
            Q0=makeQuery(id+"F1.opExtrude","CAP_FACE",FACE,{"disambiguationData":[OSD([sQuery(id+"F0.wireOp",EDGE,"E0"),sQuery(id+"F0.wireOp",EDGE,"E1"),sQuery(id+"F0.wireOp",EDGE,"E2"),sQuery(id+"F0.wireOp",EDGE,"E3"),sQuery(id+"F0.wireOp",EDGE,"E4"),sQuery(id+"F0.wireOp",EDGE,"E6"),sQuery(id+"F0.wireOp",EDGE,"E7"),sQuery(id+"F0.wireOp",EDGE,"E8"),sQuery(id+"F0.wireOp",EDGE,"E10"),sQuery(id+"F0.wireOp",EDGE,"E11")])],"isStart":true});
            var sketch = newSketch(context, id + "F9", { "sketchPlane" : qUnion([Q0])});
            skLineSegment(sketch, "E798", {"start": v(-42, -22) * mm, "end": v(-42, 0) * mm});
            skLineSegment(sketch, "E799", {"start": v(-42, 0) * mm, "end": v(0, 23) * mm});
            skLineSegment(sketch, "E800", {"start": v(0, 23) * mm, "end": v(42, 0) * mm});
            skLineSegment(sketch, "E801", {"start": v(42, 0) * mm, "end": v(42, -22) * mm});
            skLineSegment(sketch, "E802", {"start": v(42, -22) * mm, "end": v(-42, -22) * mm});
            skLineSegment(sketch, "E803", {"start": v(0, -30) * mm, "end": v(0, -10) * mm});
            skLineSegment(sketch, "E804", {"start": v(0, -10) * mm, "end": v(0, -8) * mm});
            skLineSegment(sketch, "E805", {"start": v(0, -8) * mm, "end": v(20, -8) * mm});
            skLineSegment(sketch, "E806", {"start": v(20, -8) * mm, "end": v(20, -10) * mm});
            skLineSegment(sketch, "E807", {"start": v(20, -10) * mm, "end": v(-20, -10) * mm});
            skLineSegment(sketch, "E808", {"start": v(-20, -10) * mm, "end": v(-20, -8) * mm});
            skLineSegment(sketch, "E809", {"start": v(-20, -8) * mm, "end": v(0, -8) * mm});
            skSolve(sketch);
        }
        {
            var Q0;
            Q0=makeQuery(id+"F9.imprint","IMPRINT",FACE,{"disambiguationData":[TD([[makeQuery(id+"F9.imprint","IMPRINT",EDGE,{"derivedFrom":sQuery(id+"F9.wireOp",EDGE,"E798")}),-1.0]])]});
            extrude(context, id + "F10", {"entities" : qUnion([Q0]), "operationType" : NewBodyOperationType.ADD, "oppositeDirection" : true, "depth" : 7 * mm});
        }
        {
            var Q0;
            {var subQ0=sQuery(id+"F9.wireOp",EDGE,"E804");Q0=makeQuery(id+"F9.imprint","IMPRINT",FACE,{"disambiguationData":[TD([[makeQuery(id+"F9.imprint","IMPRINT",EDGE,{"derivedFrom":subQ0}),-1.0]])]});}
            var Q1;
            {var subQ0=sQuery(id+"F9.wireOp",EDGE,"E804");Q1=makeQuery(id+"F9.imprint","IMPRINT",FACE,{"disambiguationData":[TD([[makeQuery(id+"F9.imprint","IMPRINT",EDGE,{"derivedFrom":subQ0}),1.0]])]});}
            extrude(context, id + "F11", {"entities" : qUnion([Q0, Q1]), "operationType" : NewBodyOperationType.REMOVE, "oppositeDirection" : true, "depth" : 25 * mm});
        }
        {
            var Q0;
            Q0=makeQuery(id+"F1.opExtrude","CAP_FACE",FACE,{"disambiguationData":[OSD([sQuery(id+"F0.wireOp",EDGE,"E0"),sQuery(id+"F0.wireOp",EDGE,"E1"),sQuery(id+"F0.wireOp",EDGE,"E2"),sQuery(id+"F0.wireOp",EDGE,"E3"),sQuery(id+"F0.wireOp",EDGE,"E4"),sQuery(id+"F0.wireOp",EDGE,"E6"),sQuery(id+"F0.wireOp",EDGE,"E7"),sQuery(id+"F0.wireOp",EDGE,"E8"),sQuery(id+"F0.wireOp",EDGE,"E10"),sQuery(id+"F0.wireOp",EDGE,"E11")])],"isStart":false});
            var sketch = newSketch(context, id + "F12", { "sketchPlane" : qUnion([Q0])});
            skLineSegment(sketch, "E810", {"start": v(-42, 0) * mm, "end": v(0, 23) * mm});
            skLineSegment(sketch, "E811", {"start": v(0, 23) * mm, "end": v(42, 0) * mm});
            skLineSegment(sketch, "E812", {"start": v(42, 0) * mm, "end": v(42, -22) * mm});
            skLineSegment(sketch, "E813", {"start": v(42, -22) * mm, "end": v(-42, -22) * mm});
            skLineSegment(sketch, "E814", {"start": v(-42, -22) * mm, "end": v(-42, 0) * mm});
            skSolve(sketch);
        }
        {
            var Q0;
            Q0=makeQuery(id+"F12.imprint","IMPRINT",FACE,{"disambiguationData":[TD([[makeQuery(id+"F12.imprint","IMPRINT",EDGE,{"derivedFrom":sQuery(id+"F12.wireOp",EDGE,"E810")}),1.0]])]});
            extrude(context, id + "F13", {"entities" : qUnion([Q0]), "operationType" : NewBodyOperationType.ADD, "oppositeDirection" : true, "depth" : 7 * mm});
        }
    });
